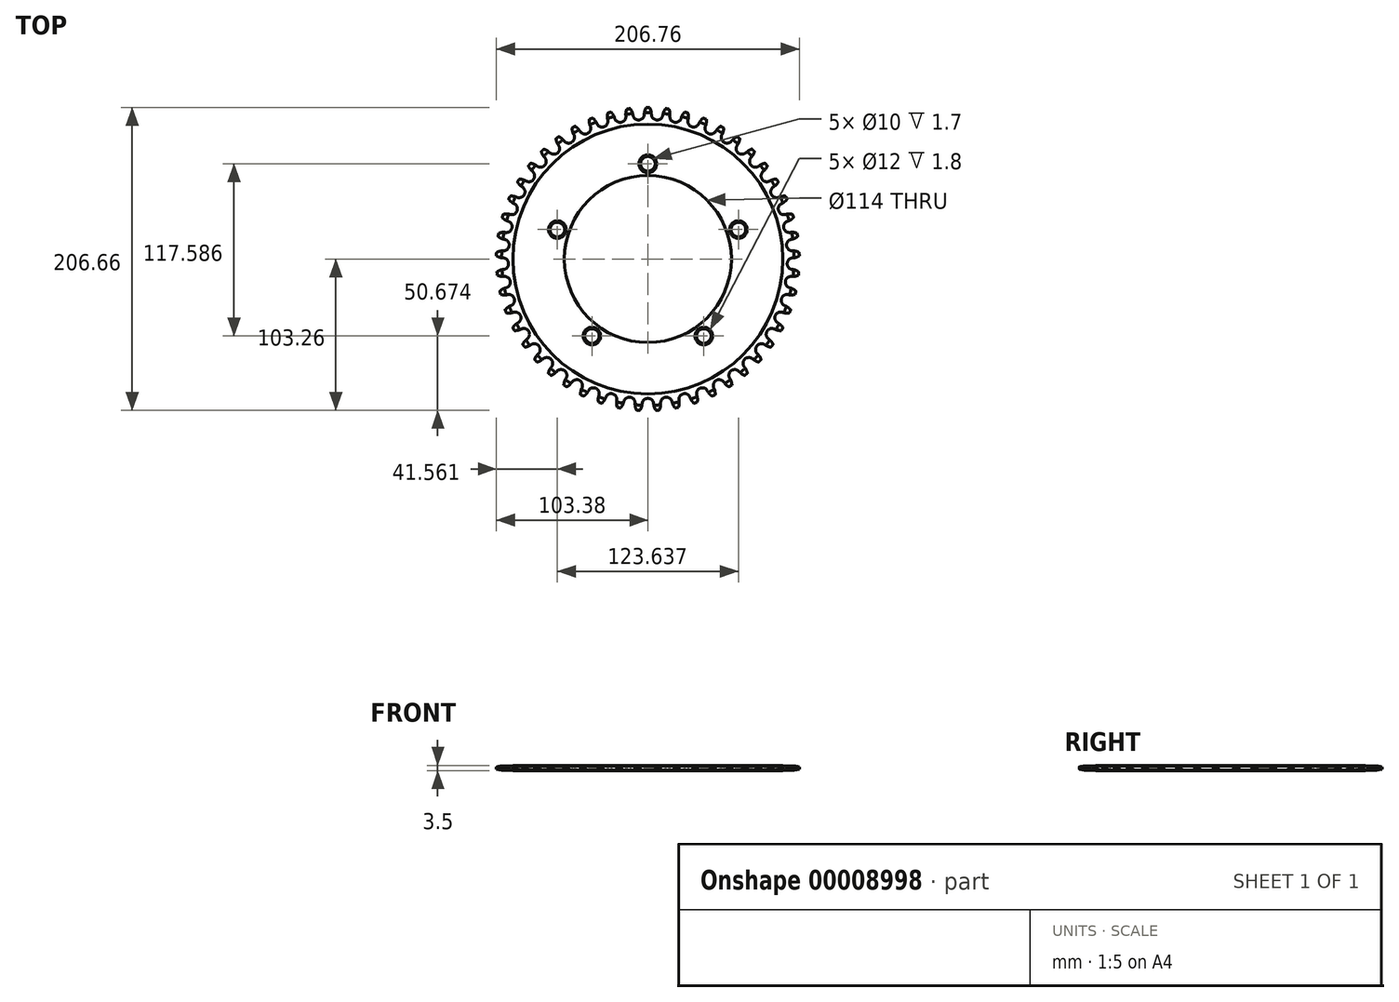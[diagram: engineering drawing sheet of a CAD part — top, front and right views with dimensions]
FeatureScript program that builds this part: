
annotation { "Feature Type Name" : "Feature", "Feature Type Description" : "" }
export const myFeature = defineFeature(function(context is Context, id is Id, definition is map)
    precondition{}
    {
        {
            var Q0;
            Q0=qCreatedBy(makeId("Top.planeOp"),FACE);
            var sketch = newSketch(context, id + "F0", { "sketchPlane" : qUnion([Q0])});
            skArc(sketch, "E0", {"start": v(2.38, 98.9) * mm, "mid": v(3.46, 96.2) * mm, "end": v(6.1, 94.95) * mm});
            skArc(sketch, "E1", {"start": v(-6.1, 94.95) * mm, "mid": v(-3.46, 96.2) * mm, "end": v(-2.38, 98.9) * mm});
            skArc(sketch, "E2", {"start": v(-1.14, 103.4) * mm, "mid": v(-2.06, 101.24) * mm, "end": v(-2.38, 98.9) * mm});
            skArc(sketch, "E3.trimOffspring", {"start": v(2.38, 98.9) * mm, "mid": v(2.06, 101.24) * mm, "end": v(1.14, 103.4) * mm});
            skLineSegment(sketch, "E4.1.1", {"start": v(-6.1, 94.95) * mm, "end": v(0, 0) * mm});
            skLineSegment(sketch, "E4.48.2", {"start": v(0, 0) * mm, "end": v(6.1, 94.95) * mm});
            skPoint(sketch, "E4.center", {"position": v(0, 0) * mm});
            skLineSegment(sketch, "E5", {"start": v(-1.14, 103.4) * mm, "end": v(1.14, 103.4) * mm});
            skPoint(sketch, "E6.orphan", {"position": v(0, 104.9) * mm});
            skLineSegment(sketch, "E7.1.0", {"start": v(0, 0) * mm, "end": v(-6.1, 94.95) * mm});
            skLineSegment(sketch, "E7.1.1", {"start": v(-18.19, 93.39) * mm, "end": v(0, 0) * mm});
            skPoint(sketch, "E7.1.2", {"position": v(-13.41, 104.04) * mm});
            skArc(sketch, "E7.1.4", {"start": v(-18.19, 93.39) * mm, "mid": v(-15.73, 94.96) * mm, "end": v(-15, 97.79) * mm});
            skArc(sketch, "E7.1.5", {"start": v(-10.29, 98.4) * mm, "mid": v(-10.9, 100.67) * mm, "end": v(-12.1, 102.7) * mm});
            skArc(sketch, "E7.1.6", {"start": v(-14.35, 102.4) * mm, "mid": v(-15, 100.14) * mm, "end": v(-15, 97.79) * mm});
            skLineSegment(sketch, "E7.1.7", {"start": v(-14.35, 102.4) * mm, "end": v(-12.1, 102.7) * mm});
            skArc(sketch, "E7.1.8", {"start": v(-10.29, 98.4) * mm, "mid": v(-8.87, 95.84) * mm, "end": v(-6.1, 94.95) * mm});
            skLineSegment(sketch, "E7.2.0", {"start": v(0, 0) * mm, "end": v(-18.19, 93.39) * mm});
            skLineSegment(sketch, "E7.2.1", {"start": v(-29.98, 90.3) * mm, "end": v(0, 0) * mm});
            skPoint(sketch, "E7.2.2", {"position": v(-26.6, 101.47) * mm});
            skArc(sketch, "E7.2.4", {"start": v(-29.98, 90.3) * mm, "mid": v(-27.74, 92.17) * mm, "end": v(-27.4, 95.07) * mm});
            skArc(sketch, "E7.2.5", {"start": v(-22.78, 96.28) * mm, "mid": v(-23.68, 98.45) * mm, "end": v(-25.13, 100.3) * mm});
            skArc(sketch, "E7.2.6", {"start": v(-27.33, 99.73) * mm, "mid": v(-27.68, 97.4) * mm, "end": v(-27.4, 95.07) * mm});
            skLineSegment(sketch, "E7.2.7", {"start": v(-27.33, 99.73) * mm, "end": v(-25.13, 100.3) * mm});
            skArc(sketch, "E7.2.8", {"start": v(-22.78, 96.28) * mm, "mid": v(-21.06, 93.92) * mm, "end": v(-18.19, 93.39) * mm});
            skLineSegment(sketch, "E7.3.0", {"start": v(0, 0) * mm, "end": v(-29.98, 90.3) * mm});
            skLineSegment(sketch, "E7.3.1", {"start": v(-41.28, 85.72) * mm, "end": v(0, 0) * mm});
            skPoint(sketch, "E7.3.2", {"position": v(-39.37, 97.23) * mm});
            skArc(sketch, "E7.3.4", {"start": v(-41.28, 85.72) * mm, "mid": v(-39.3, 87.86) * mm, "end": v(-39.32, 90.78) * mm});
            skArc(sketch, "E7.3.5", {"start": v(-34.9, 92.57) * mm, "mid": v(-36.08, 94.61) * mm, "end": v(-37.75, 96.27) * mm});
            skArc(sketch, "E7.3.6", {"start": v(-39.86, 95.42) * mm, "mid": v(-39.9, 93.06) * mm, "end": v(-39.32, 90.78) * mm});
            skLineSegment(sketch, "E7.3.7", {"start": v(-39.86, 95.42) * mm, "end": v(-37.75, 96.27) * mm});
            skArc(sketch, "E7.3.8", {"start": v(-34.9, 92.57) * mm, "mid": v(-32.9, 90.46) * mm, "end": v(-29.98, 90.3) * mm});
            skLineSegment(sketch, "E7.4.0", {"start": v(0, 0) * mm, "end": v(-41.28, 85.72) * mm});
            skLineSegment(sketch, "E7.4.1", {"start": v(-51.9, 79.74) * mm, "end": v(0, 0) * mm});
            skPoint(sketch, "E7.4.2", {"position": v(-51.48, 91.4) * mm});
            skArc(sketch, "E7.4.4", {"start": v(-51.9, 79.74) * mm, "mid": v(-50.21, 82.12) * mm, "end": v(-50.6, 85.01) * mm});
            skArc(sketch, "E7.4.5", {"start": v(-46.46, 87.35) * mm, "mid": v(-47.88, 89.22) * mm, "end": v(-49.75, 90.65) * mm});
            skArc(sketch, "E7.4.6", {"start": v(-51.73, 89.54) * mm, "mid": v(-51.48, 87.2) * mm, "end": v(-50.6, 85.01) * mm});
            skLineSegment(sketch, "E7.4.7", {"start": v(-51.73, 89.54) * mm, "end": v(-49.75, 90.65) * mm});
            skArc(sketch, "E7.4.8", {"start": v(-46.46, 87.35) * mm, "mid": v(-44.2, 85.5) * mm, "end": v(-41.28, 85.72) * mm});
            skLineSegment(sketch, "E7.5.0", {"start": v(0, 0) * mm, "end": v(-51.9, 79.74) * mm});
            skLineSegment(sketch, "E7.5.1", {"start": v(-61.67, 72.44) * mm, "end": v(0, 0) * mm});
            skPoint(sketch, "E7.5.2", {"position": v(-62.74, 84.07) * mm});
            skArc(sketch, "E7.5.4", {"start": v(-61.67, 72.44) * mm, "mid": v(-60.3, 75.02) * mm, "end": v(-61.07, 77.84) * mm});
            skArc(sketch, "E7.5.5", {"start": v(-57.25, 80.69) * mm, "mid": v(-58.9, 82.37) * mm, "end": v(-60.93, 83.55) * mm});
            skArc(sketch, "E7.5.6", {"start": v(-62.76, 82.19) * mm, "mid": v(-62.2, 79.9) * mm, "end": v(-61.07, 77.84) * mm});
            skLineSegment(sketch, "E7.5.7", {"start": v(-62.76, 82.19) * mm, "end": v(-60.93, 83.55) * mm});
            skArc(sketch, "E7.5.8", {"start": v(-57.25, 80.69) * mm, "mid": v(-54.76, 79.16) * mm, "end": v(-51.9, 79.74) * mm});
            skLineSegment(sketch, "E7.6.0", {"start": v(0, 0) * mm, "end": v(-61.67, 72.44) * mm});
            skLineSegment(sketch, "E7.6.1", {"start": v(-70.43, 63.96) * mm, "end": v(0, 0) * mm});
            skPoint(sketch, "E7.6.2", {"position": v(-72.98, 75.35) * mm});
            skArc(sketch, "E7.6.4", {"start": v(-70.43, 63.96) * mm, "mid": v(-69.4, 66.7) * mm, "end": v(-70.52, 69.4) * mm});
            skArc(sketch, "E7.6.5", {"start": v(-67.1, 72.7) * mm, "mid": v(-68.95, 74.16) * mm, "end": v(-71.12, 75.07) * mm});
            skArc(sketch, "E7.6.6", {"start": v(-72.75, 73.49) * mm, "mid": v(-71.91, 71.29) * mm, "end": v(-70.52, 69.4) * mm});
            skLineSegment(sketch, "E7.6.7", {"start": v(-72.75, 73.49) * mm, "end": v(-71.12, 75.07) * mm});
            skArc(sketch, "E7.6.8", {"start": v(-67.1, 72.7) * mm, "mid": v(-64.44, 71.5) * mm, "end": v(-61.67, 72.44) * mm});
            skLineSegment(sketch, "E7.7.0", {"start": v(0, 0) * mm, "end": v(-70.43, 63.96) * mm});
            skLineSegment(sketch, "E7.7.1", {"start": v(-78.03, 54.43) * mm, "end": v(0, 0) * mm});
            skPoint(sketch, "E7.7.2", {"position": v(-82.01, 65.4) * mm});
            skArc(sketch, "E7.7.4", {"start": v(-78.03, 54.43) * mm, "mid": v(-77.36, 57.27) * mm, "end": v(-78.81, 59.8) * mm});
            skArc(sketch, "E7.7.5", {"start": v(-75.84, 63.53) * mm, "mid": v(-77.86, 64.73) * mm, "end": v(-80.13, 65.36) * mm});
            skArc(sketch, "E7.7.6", {"start": v(-81.55, 63.58) * mm, "mid": v(-80.44, 61.5) * mm, "end": v(-78.81, 59.8) * mm});
            skLineSegment(sketch, "E7.7.7", {"start": v(-81.55, 63.58) * mm, "end": v(-80.13, 65.36) * mm});
            skArc(sketch, "E7.7.8", {"start": v(-75.84, 63.53) * mm, "mid": v(-73.05, 62.68) * mm, "end": v(-70.43, 63.96) * mm});
            skLineSegment(sketch, "E7.8.0", {"start": v(0, 0) * mm, "end": v(-78.03, 54.43) * mm});
            skLineSegment(sketch, "E7.8.1", {"start": v(-84.35, 44) * mm, "end": v(0, 0) * mm});
            skPoint(sketch, "E7.8.2", {"position": v(-89.7, 54.38) * mm});
            skArc(sketch, "E7.8.4", {"start": v(-84.35, 44) * mm, "mid": v(-84.05, 46.91) * mm, "end": v(-85.81, 49.24) * mm});
            skArc(sketch, "E7.8.5", {"start": v(-83.34, 53.3) * mm, "mid": v(-85.5, 54.25) * mm, "end": v(-87.83, 54.57) * mm});
            skArc(sketch, "E7.8.6", {"start": v(-89.01, 52.63) * mm, "mid": v(-87.64, 50.72) * mm, "end": v(-85.81, 49.24) * mm});
            skLineSegment(sketch, "E7.8.7", {"start": v(-89.01, 52.63) * mm, "end": v(-87.83, 54.57) * mm});
            skArc(sketch, "E7.8.8", {"start": v(-83.34, 53.3) * mm, "mid": v(-80.47, 52.82) * mm, "end": v(-78.03, 54.43) * mm});
            skLineSegment(sketch, "E7.9.0", {"start": v(0, 0) * mm, "end": v(-84.35, 44) * mm});
            skLineSegment(sketch, "E7.9.1", {"start": v(-89.29, 32.86) * mm, "end": v(0, 0) * mm});
            skPoint(sketch, "E7.9.2", {"position": v(-95.92, 42.46) * mm});
            skArc(sketch, "E7.9.4", {"start": v(-89.29, 32.86) * mm, "mid": v(-89.36, 35.78) * mm, "end": v(-91.4, 37.86) * mm});
            skArc(sketch, "E7.9.5", {"start": v(-89.48, 42.21) * mm, "mid": v(-91.74, 42.87) * mm, "end": v(-94.09, 42.9) * mm});
            skArc(sketch, "E7.9.6", {"start": v(-95, 40.81) * mm, "mid": v(-93.4, 39.1) * mm, "end": v(-91.4, 37.86) * mm});
            skLineSegment(sketch, "E7.9.7", {"start": v(-95, 40.81) * mm, "end": v(-94.09, 42.9) * mm});
            skArc(sketch, "E7.9.8", {"start": v(-89.48, 42.21) * mm, "mid": v(-86.56, 42.1) * mm, "end": v(-84.35, 44) * mm});
            skLineSegment(sketch, "E7.10.0", {"start": v(0, 0) * mm, "end": v(-89.29, 32.86) * mm});
            skLineSegment(sketch, "E7.10.1", {"start": v(-92.76, 21.17) * mm, "end": v(0, 0) * mm});
            skPoint(sketch, "E7.10.2", {"position": v(-100.56, 29.85) * mm});
            skArc(sketch, "E7.10.4", {"start": v(-92.76, 21.17) * mm, "mid": v(-93.2, 24.06) * mm, "end": v(-95.5, 25.86) * mm});
            skArc(sketch, "E7.10.5", {"start": v(-94.14, 30.42) * mm, "mid": v(-96.47, 30.78) * mm, "end": v(-98.8, 30.5) * mm});
            skArc(sketch, "E7.10.6", {"start": v(-99.45, 28.33) * mm, "mid": v(-97.64, 26.83) * mm, "end": v(-95.5, 25.86) * mm});
            skLineSegment(sketch, "E7.10.7", {"start": v(-99.45, 28.33) * mm, "end": v(-98.8, 30.5) * mm});
            skArc(sketch, "E7.10.8", {"start": v(-94.14, 30.42) * mm, "mid": v(-91.23, 30.68) * mm, "end": v(-89.29, 32.86) * mm});
            skLineSegment(sketch, "E7.11.0", {"start": v(0, 0) * mm, "end": v(-92.76, 21.17) * mm});
            skLineSegment(sketch, "E7.11.1", {"start": v(-94.7, 9.14) * mm, "end": v(0, 0) * mm});
            skPoint(sketch, "E7.11.2", {"position": v(-103.55, 16.74) * mm});
            skArc(sketch, "E7.11.4", {"start": v(-94.7, 9.14) * mm, "mid": v(-95.5, 11.94) * mm, "end": v(-98.02, 13.43) * mm});
            skArc(sketch, "E7.11.5", {"start": v(-97.26, 18.14) * mm, "mid": v(-99.61, 18.2) * mm, "end": v(-101.9, 17.62) * mm});
            skArc(sketch, "E7.11.6", {"start": v(-102.26, 15.38) * mm, "mid": v(-100.27, 14.12) * mm, "end": v(-98.02, 13.43) * mm});
            skLineSegment(sketch, "E7.11.7", {"start": v(-102.26, 15.38) * mm, "end": v(-101.9, 17.62) * mm});
            skArc(sketch, "E7.11.8", {"start": v(-97.26, 18.14) * mm, "mid": v(-94.4, 18.76) * mm, "end": v(-92.76, 21.17) * mm});
            skLineSegment(sketch, "E7.12.0", {"start": v(0, 0) * mm, "end": v(-94.7, 9.14) * mm});
            skLineSegment(sketch, "E7.12.1", {"start": v(-95.1, -3.05) * mm, "end": v(0, 0) * mm});
            skPoint(sketch, "E7.12.2", {"position": v(-104.85, 3.36) * mm});
            skArc(sketch, "E7.12.4", {"start": v(-95.1, -3.05) * mm, "mid": v(-96.25, -0.37) * mm, "end": v(-98.93, 0.8) * mm});
            skArc(sketch, "E7.12.5", {"start": v(-98.78, 5.55) * mm, "mid": v(-101.12, 5.3) * mm, "end": v(-103.3, 4.45) * mm});
            skArc(sketch, "E7.12.6", {"start": v(-103.38, 2.18) * mm, "mid": v(-101.25, 1.18) * mm, "end": v(-98.93, 0.8) * mm});
            skLineSegment(sketch, "E7.12.7", {"start": v(-103.38, 2.18) * mm, "end": v(-103.3, 4.45) * mm});
            skArc(sketch, "E7.12.8", {"start": v(-98.78, 5.55) * mm, "mid": v(-96.03, 6.54) * mm, "end": v(-94.7, 9.14) * mm});
            skLineSegment(sketch, "E7.13.0", {"start": v(0, 0) * mm, "end": v(-95.1, -3.05) * mm});
            skLineSegment(sketch, "E7.13.1", {"start": v(-93.92, -15.18) * mm, "end": v(0, 0) * mm});
            skPoint(sketch, "E7.13.2", {"position": v(-104.41, -10.07) * mm});
            skArc(sketch, "E7.13.4", {"start": v(-93.92, -15.18) * mm, "mid": v(-95.42, -12.68) * mm, "end": v(-98.22, -11.87) * mm});
            skArc(sketch, "E7.13.5", {"start": v(-98.68, -7.13) * mm, "mid": v(-100.97, -7.67) * mm, "end": v(-103.03, -8.8) * mm});
            skArc(sketch, "E7.13.6", {"start": v(-102.81, -11.06) * mm, "mid": v(-100.57, -11.78) * mm, "end": v(-98.22, -11.87) * mm});
            skLineSegment(sketch, "E7.13.7", {"start": v(-102.81, -11.06) * mm, "end": v(-103.03, -8.8) * mm});
            skArc(sketch, "E7.13.8", {"start": v(-98.68, -7.13) * mm, "mid": v(-96.08, -5.8) * mm, "end": v(-95.1, -3.05) * mm});
            skLineSegment(sketch, "E7.14.0", {"start": v(0, 0) * mm, "end": v(-93.92, -15.18) * mm});
            skLineSegment(sketch, "E7.14.1", {"start": v(-91.2, -27.07) * mm, "end": v(0, 0) * mm});
            skPoint(sketch, "E7.14.2", {"position": v(-102.27, -23.34) * mm});
            skArc(sketch, "E7.14.4", {"start": v(-91.2, -27.07) * mm, "mid": v(-93.01, -24.77) * mm, "end": v(-95.9, -24.33) * mm});
            skArc(sketch, "E7.14.5", {"start": v(-96.96, -19.69) * mm, "mid": v(-99.16, -20.51) * mm, "end": v(-101.06, -21.9) * mm});
            skArc(sketch, "E7.14.6", {"start": v(-100.55, -24.12) * mm, "mid": v(-98.24, -24.54) * mm, "end": v(-95.9, -24.33) * mm});
            skLineSegment(sketch, "E7.14.7", {"start": v(-100.55, -24.12) * mm, "end": v(-101.06, -21.9) * mm});
            skArc(sketch, "E7.14.8", {"start": v(-96.96, -19.69) * mm, "mid": v(-94.55, -18.04) * mm, "end": v(-93.92, -15.18) * mm});
            skLineSegment(sketch, "E7.15.0", {"start": v(0, 0) * mm, "end": v(-91.2, -27.07) * mm});
            skLineSegment(sketch, "E7.15.1", {"start": v(-87, -38.51) * mm, "end": v(0, 0) * mm});
            skPoint(sketch, "E7.15.2", {"position": v(-98.44, -36.23) * mm});
            skArc(sketch, "E7.15.4", {"start": v(-87, -38.51) * mm, "mid": v(-89.08, -36.46) * mm, "end": v(-92, -36.4) * mm});
            skArc(sketch, "E7.15.5", {"start": v(-93.64, -31.92) * mm, "mid": v(-95.72, -33.03) * mm, "end": v(-97.43, -34.64) * mm});
            skArc(sketch, "E7.15.6", {"start": v(-96.64, -36.78) * mm, "mid": v(-94.3, -36.9) * mm, "end": v(-92, -36.4) * mm});
            skLineSegment(sketch, "E7.15.7", {"start": v(-96.64, -36.78) * mm, "end": v(-97.43, -34.64) * mm});
            skArc(sketch, "E7.15.8", {"start": v(-93.64, -31.92) * mm, "mid": v(-91.47, -29.98) * mm, "end": v(-91.2, -27.07) * mm});
            skLineSegment(sketch, "E7.16.0", {"start": v(0, 0) * mm, "end": v(-87, -38.51) * mm});
            skLineSegment(sketch, "E7.16.1", {"start": v(-81.36, -49.32) * mm, "end": v(0, 0) * mm});
            skPoint(sketch, "E7.16.2", {"position": v(-93, -48.52) * mm});
            skArc(sketch, "E7.16.4", {"start": v(-81.36, -49.32) * mm, "mid": v(-83.69, -47.56) * mm, "end": v(-86.59, -47.86) * mm});
            skArc(sketch, "E7.16.5", {"start": v(-88.8, -43.64) * mm, "mid": v(-90.71, -45) * mm, "end": v(-92.2, -46.82) * mm});
            skArc(sketch, "E7.16.6", {"start": v(-91.15, -48.83) * mm, "mid": v(-88.8, -48.66) * mm, "end": v(-86.59, -47.86) * mm});
            skLineSegment(sketch, "E7.16.7", {"start": v(-91.15, -48.83) * mm, "end": v(-92.2, -46.82) * mm});
            skArc(sketch, "E7.16.8", {"start": v(-88.8, -43.64) * mm, "mid": v(-86.88, -41.43) * mm, "end": v(-87, -38.51) * mm});
            skLineSegment(sketch, "E7.17.0", {"start": v(0, 0) * mm, "end": v(-81.36, -49.32) * mm});
            skLineSegment(sketch, "E7.17.1", {"start": v(-74.38, -59.32) * mm, "end": v(0, 0) * mm});
            skPoint(sketch, "E7.17.2", {"position": v(-86.04, -60.01) * mm});
            skArc(sketch, "E7.17.4", {"start": v(-74.38, -59.32) * mm, "mid": v(-76.92, -57.87) * mm, "end": v(-79.76, -58.54) * mm});
            skArc(sketch, "E7.17.5", {"start": v(-82.48, -54.63) * mm, "mid": v(-84.21, -56.23) * mm, "end": v(-85.46, -58.22) * mm});
            skArc(sketch, "E7.17.6", {"start": v(-84.15, -60.09) * mm, "mid": v(-81.85, -59.61) * mm, "end": v(-79.76, -58.54) * mm});
            skLineSegment(sketch, "E7.17.7", {"start": v(-84.15, -60.09) * mm, "end": v(-85.46, -58.22) * mm});
            skArc(sketch, "E7.17.8", {"start": v(-82.48, -54.63) * mm, "mid": v(-80.87, -52.2) * mm, "end": v(-81.36, -49.32) * mm});
            skLineSegment(sketch, "E7.18.0", {"start": v(0, 0) * mm, "end": v(-74.38, -59.32) * mm});
            skLineSegment(sketch, "E7.18.1", {"start": v(-66.19, -68.34) * mm, "end": v(0, 0) * mm});
            skPoint(sketch, "E7.18.2", {"position": v(-77.65, -70.52) * mm});
            skArc(sketch, "E7.18.4", {"start": v(-66.19, -68.34) * mm, "mid": v(-68.89, -67.23) * mm, "end": v(-71.62, -68.26) * mm});
            skArc(sketch, "E7.18.5", {"start": v(-74.82, -64.73) * mm, "mid": v(-76.33, -66.53) * mm, "end": v(-77.3, -68.67) * mm});
            skArc(sketch, "E7.18.6", {"start": v(-75.78, -70.36) * mm, "mid": v(-73.56, -69.6) * mm, "end": v(-71.62, -68.26) * mm});
            skLineSegment(sketch, "E7.18.7", {"start": v(-75.78, -70.36) * mm, "end": v(-77.3, -68.67) * mm});
            skArc(sketch, "E7.18.8", {"start": v(-74.82, -64.73) * mm, "mid": v(-73.53, -62.11) * mm, "end": v(-74.38, -59.32) * mm});
            skLineSegment(sketch, "E7.19.0", {"start": v(0, 0) * mm, "end": v(-66.19, -68.34) * mm});
            skLineSegment(sketch, "E7.19.1", {"start": v(-56.9, -76.25) * mm, "end": v(0, 0) * mm});
            skPoint(sketch, "E7.19.2", {"position": v(-68, -79.87) * mm});
            skArc(sketch, "E7.19.4", {"start": v(-56.9, -76.25) * mm, "mid": v(-59.72, -75.48) * mm, "end": v(-62.3, -76.86) * mm});
            skArc(sketch, "E7.19.5", {"start": v(-65.93, -73.77) * mm, "mid": v(-67.2, -75.75) * mm, "end": v(-67.9, -78) * mm});
            skArc(sketch, "E7.19.6", {"start": v(-66.16, -79.47) * mm, "mid": v(-64.05, -78.42) * mm, "end": v(-62.3, -76.86) * mm});
            skLineSegment(sketch, "E7.19.7", {"start": v(-66.16, -79.47) * mm, "end": v(-67.9, -78) * mm});
            skArc(sketch, "E7.19.8", {"start": v(-65.93, -73.77) * mm, "mid": v(-64.98, -71) * mm, "end": v(-66.19, -68.34) * mm});
            skLineSegment(sketch, "E7.20.0", {"start": v(0, 0) * mm, "end": v(-56.9, -76.25) * mm});
            skLineSegment(sketch, "E7.20.1", {"start": v(-46.69, -82.9) * mm, "end": v(0, 0) * mm});
            skPoint(sketch, "E7.20.2", {"position": v(-57.23, -87.91) * mm});
            skArc(sketch, "E7.20.4", {"start": v(-46.69, -82.9) * mm, "mid": v(-49.58, -82.5) * mm, "end": v(-51.96, -84.2) * mm});
            skArc(sketch, "E7.20.5", {"start": v(-55.95, -81.6) * mm, "mid": v(-56.96, -83.72) * mm, "end": v(-57.36, -86.04) * mm});
            skArc(sketch, "E7.20.6", {"start": v(-55.46, -87.28) * mm, "mid": v(-53.5, -85.97) * mm, "end": v(-51.96, -84.2) * mm});
            skLineSegment(sketch, "E7.20.7", {"start": v(-55.46, -87.28) * mm, "end": v(-57.36, -86.04) * mm});
            skArc(sketch, "E7.20.8", {"start": v(-55.95, -81.6) * mm, "mid": v(-55.37, -78.73) * mm, "end": v(-56.9, -76.25) * mm});
            skLineSegment(sketch, "E7.21.0", {"start": v(0, 0) * mm, "end": v(-46.69, -82.9) * mm});
            skLineSegment(sketch, "E7.21.1", {"start": v(-35.7, -88.19) * mm, "end": v(0, 0) * mm});
            skPoint(sketch, "E7.21.2", {"position": v(-45.51, -94.51) * mm});
            skArc(sketch, "E7.21.4", {"start": v(-35.7, -88.19) * mm, "mid": v(-38.62, -88.16) * mm, "end": v(-40.77, -90.14) * mm});
            skArc(sketch, "E7.21.5", {"start": v(-45.06, -88.08) * mm, "mid": v(-45.79, -90.32) * mm, "end": v(-45.89, -92.67) * mm});
            skArc(sketch, "E7.21.6", {"start": v(-43.84, -93.65) * mm, "mid": v(-42.07, -92.1) * mm, "end": v(-40.77, -90.14) * mm});
            skLineSegment(sketch, "E7.21.7", {"start": v(-43.84, -93.65) * mm, "end": v(-45.89, -92.67) * mm});
            skArc(sketch, "E7.21.8", {"start": v(-45.06, -88.08) * mm, "mid": v(-44.85, -85.17) * mm, "end": v(-46.69, -82.9) * mm});
            skLineSegment(sketch, "E7.22.0", {"start": v(0, 0) * mm, "end": v(-35.7, -88.19) * mm});
            skLineSegment(sketch, "E7.22.1", {"start": v(-24.13, -92.03) * mm, "end": v(0, 0) * mm});
            skPoint(sketch, "E7.22.2", {"position": v(-33.05, -99.56) * mm});
            skArc(sketch, "E7.22.4", {"start": v(-24.13, -92.03) * mm, "mid": v(-27.03, -92.38) * mm, "end": v(-28.9, -94.62) * mm});
            skArc(sketch, "E7.22.5", {"start": v(-33.43, -93.12) * mm, "mid": v(-33.86, -95.43) * mm, "end": v(-33.66, -97.77) * mm});
            skArc(sketch, "E7.22.6", {"start": v(-31.5, -98.49) * mm, "mid": v(-29.94, -96.73) * mm, "end": v(-28.9, -94.62) * mm});
            skLineSegment(sketch, "E7.22.7", {"start": v(-31.5, -98.49) * mm, "end": v(-33.66, -97.77) * mm});
            skArc(sketch, "E7.22.8", {"start": v(-33.43, -93.12) * mm, "mid": v(-33.59, -90.2) * mm, "end": v(-35.7, -88.19) * mm});
            skLineSegment(sketch, "E7.23.0", {"start": v(0, 0) * mm, "end": v(-24.13, -92.03) * mm});
            skLineSegment(sketch, "E7.23.1", {"start": v(-12.17, -94.36) * mm, "end": v(0, 0) * mm});
            skPoint(sketch, "E7.23.2", {"position": v(-20.05, -102.96) * mm});
            skArc(sketch, "E7.23.4", {"start": v(-12.17, -94.36) * mm, "mid": v(-15, -95.08) * mm, "end": v(-16.57, -97.54) * mm});
            skArc(sketch, "E7.23.5", {"start": v(-21.24, -96.63) * mm, "mid": v(-21.38, -98.98) * mm, "end": v(-20.88, -101.28) * mm});
            skArc(sketch, "E7.23.6", {"start": v(-18.65, -101.7) * mm, "mid": v(-17.33, -99.77) * mm, "end": v(-16.57, -97.54) * mm});
            skLineSegment(sketch, "E7.23.7", {"start": v(-18.65, -101.7) * mm, "end": v(-20.88, -101.28) * mm});
            skArc(sketch, "E7.23.8", {"start": v(-21.24, -96.63) * mm, "mid": v(-21.78, -93.76) * mm, "end": v(-24.13, -92.03) * mm});
            skLineSegment(sketch, "E7.24.0", {"start": v(0, 0) * mm, "end": v(-12.17, -94.36) * mm});
            skLineSegment(sketch, "E7.24.1", {"start": v(0, -95.14) * mm, "end": v(0, 0) * mm});
            skPoint(sketch, "E7.24.2", {"position": v(-6.72, -104.68) * mm});
            skArc(sketch, "E7.24.4", {"start": v(0, -95.14) * mm, "mid": v(-2.71, -96.22) * mm, "end": v(-3.96, -98.86) * mm});
            skArc(sketch, "E7.24.5", {"start": v(-8.71, -98.55) * mm, "mid": v(-8.55, -100.9) * mm, "end": v(-7.76, -103.11) * mm});
            skArc(sketch, "E7.24.6", {"start": v(-5.5, -103.26) * mm, "mid": v(-4.43, -101.16) * mm, "end": v(-3.96, -98.86) * mm});
            skLineSegment(sketch, "E7.24.7", {"start": v(-5.5, -103.26) * mm, "end": v(-7.76, -103.11) * mm});
            skArc(sketch, "E7.24.8", {"start": v(-8.71, -98.55) * mm, "mid": v(-9.61, -95.77) * mm, "end": v(-12.17, -94.36) * mm});
            skLineSegment(sketch, "E7.25.0", {"start": v(0, 0) * mm, "end": v(0, -95.14) * mm});
            skLineSegment(sketch, "E7.25.1", {"start": v(12.17, -94.36) * mm, "end": v(0, 0) * mm});
            skPoint(sketch, "E7.25.2", {"position": v(6.72, -104.68) * mm});
            skArc(sketch, "E7.25.4", {"start": v(12.17, -94.36) * mm, "mid": v(9.61, -95.77) * mm, "end": v(8.71, -98.55) * mm});
            skArc(sketch, "E7.25.5", {"start": v(3.96, -98.86) * mm, "mid": v(4.43, -101.16) * mm, "end": v(5.5, -103.26) * mm});
            skArc(sketch, "E7.25.6", {"start": v(7.76, -103.11) * mm, "mid": v(8.55, -100.9) * mm, "end": v(8.71, -98.55) * mm});
            skLineSegment(sketch, "E7.25.7", {"start": v(7.76, -103.11) * mm, "end": v(5.5, -103.26) * mm});
            skArc(sketch, "E7.25.8", {"start": v(3.96, -98.86) * mm, "mid": v(2.71, -96.22) * mm, "end": v(0, -95.14) * mm});
            skLineSegment(sketch, "E7.26.0", {"start": v(0, 0) * mm, "end": v(12.17, -94.36) * mm});
            skLineSegment(sketch, "E7.26.1", {"start": v(24.13, -92.03) * mm, "end": v(0, 0) * mm});
            skPoint(sketch, "E7.26.2", {"position": v(20.05, -102.96) * mm});
            skArc(sketch, "E7.26.4", {"start": v(24.13, -92.03) * mm, "mid": v(21.78, -93.76) * mm, "end": v(21.24, -96.63) * mm});
            skArc(sketch, "E7.26.5", {"start": v(16.57, -97.54) * mm, "mid": v(17.33, -99.77) * mm, "end": v(18.65, -101.7) * mm});
            skArc(sketch, "E7.26.6", {"start": v(20.88, -101.28) * mm, "mid": v(21.38, -98.98) * mm, "end": v(21.24, -96.63) * mm});
            skLineSegment(sketch, "E7.26.7", {"start": v(20.88, -101.28) * mm, "end": v(18.65, -101.7) * mm});
            skArc(sketch, "E7.26.8", {"start": v(16.57, -97.54) * mm, "mid": v(15, -95.08) * mm, "end": v(12.17, -94.36) * mm});
            skLineSegment(sketch, "E7.27.0", {"start": v(0, 0) * mm, "end": v(24.13, -92.03) * mm});
            skLineSegment(sketch, "E7.27.1", {"start": v(35.7, -88.19) * mm, "end": v(0, 0) * mm});
            skPoint(sketch, "E7.27.2", {"position": v(33.05, -99.56) * mm});
            skArc(sketch, "E7.27.4", {"start": v(35.7, -88.19) * mm, "mid": v(33.59, -90.2) * mm, "end": v(33.43, -93.12) * mm});
            skArc(sketch, "E7.27.5", {"start": v(28.9, -94.62) * mm, "mid": v(29.94, -96.73) * mm, "end": v(31.5, -98.49) * mm});
            skArc(sketch, "E7.27.6", {"start": v(33.66, -97.77) * mm, "mid": v(33.86, -95.43) * mm, "end": v(33.43, -93.12) * mm});
            skLineSegment(sketch, "E7.27.7", {"start": v(33.66, -97.77) * mm, "end": v(31.5, -98.49) * mm});
            skArc(sketch, "E7.27.8", {"start": v(28.9, -94.62) * mm, "mid": v(27.03, -92.38) * mm, "end": v(24.13, -92.03) * mm});
            skLineSegment(sketch, "E7.28.0", {"start": v(0, 0) * mm, "end": v(35.7, -88.19) * mm});
            skLineSegment(sketch, "E7.28.1", {"start": v(46.69, -82.9) * mm, "end": v(0, 0) * mm});
            skPoint(sketch, "E7.28.2", {"position": v(45.51, -94.51) * mm});
            skArc(sketch, "E7.28.4", {"start": v(46.69, -82.9) * mm, "mid": v(44.85, -85.17) * mm, "end": v(45.06, -88.08) * mm});
            skArc(sketch, "E7.28.5", {"start": v(40.77, -90.14) * mm, "mid": v(42.07, -92.1) * mm, "end": v(43.84, -93.65) * mm});
            skArc(sketch, "E7.28.6", {"start": v(45.89, -92.67) * mm, "mid": v(45.79, -90.32) * mm, "end": v(45.06, -88.08) * mm});
            skLineSegment(sketch, "E7.28.7", {"start": v(45.89, -92.67) * mm, "end": v(43.84, -93.65) * mm});
            skArc(sketch, "E7.28.8", {"start": v(40.77, -90.14) * mm, "mid": v(38.62, -88.16) * mm, "end": v(35.7, -88.19) * mm});
            skLineSegment(sketch, "E7.29.0", {"start": v(0, 0) * mm, "end": v(46.69, -82.9) * mm});
            skLineSegment(sketch, "E7.29.1", {"start": v(56.9, -76.25) * mm, "end": v(0, 0) * mm});
            skPoint(sketch, "E7.29.2", {"position": v(57.23, -87.91) * mm});
            skArc(sketch, "E7.29.4", {"start": v(56.9, -76.25) * mm, "mid": v(55.37, -78.73) * mm, "end": v(55.95, -81.6) * mm});
            skArc(sketch, "E7.29.5", {"start": v(51.96, -84.2) * mm, "mid": v(53.5, -85.97) * mm, "end": v(55.46, -87.28) * mm});
            skArc(sketch, "E7.29.6", {"start": v(57.36, -86.04) * mm, "mid": v(56.96, -83.72) * mm, "end": v(55.95, -81.6) * mm});
            skLineSegment(sketch, "E7.29.7", {"start": v(57.36, -86.04) * mm, "end": v(55.46, -87.28) * mm});
            skArc(sketch, "E7.29.8", {"start": v(51.96, -84.2) * mm, "mid": v(49.58, -82.5) * mm, "end": v(46.69, -82.9) * mm});
            skLineSegment(sketch, "E7.30.0", {"start": v(0, 0) * mm, "end": v(56.9, -76.25) * mm});
            skLineSegment(sketch, "E7.30.1", {"start": v(66.19, -68.34) * mm, "end": v(0, 0) * mm});
            skPoint(sketch, "E7.30.2", {"position": v(68, -79.87) * mm});
            skArc(sketch, "E7.30.4", {"start": v(66.19, -68.34) * mm, "mid": v(64.98, -71) * mm, "end": v(65.93, -73.77) * mm});
            skArc(sketch, "E7.30.5", {"start": v(62.3, -76.86) * mm, "mid": v(64.05, -78.42) * mm, "end": v(66.16, -79.47) * mm});
            skArc(sketch, "E7.30.6", {"start": v(67.9, -78) * mm, "mid": v(67.2, -75.75) * mm, "end": v(65.93, -73.77) * mm});
            skLineSegment(sketch, "E7.30.7", {"start": v(67.9, -78) * mm, "end": v(66.16, -79.47) * mm});
            skArc(sketch, "E7.30.8", {"start": v(62.3, -76.86) * mm, "mid": v(59.72, -75.48) * mm, "end": v(56.9, -76.25) * mm});
            skLineSegment(sketch, "E7.31.0", {"start": v(0, 0) * mm, "end": v(66.19, -68.34) * mm});
            skLineSegment(sketch, "E7.31.1", {"start": v(74.38, -59.32) * mm, "end": v(0, 0) * mm});
            skPoint(sketch, "E7.31.2", {"position": v(77.65, -70.52) * mm});
            skArc(sketch, "E7.31.4", {"start": v(74.38, -59.32) * mm, "mid": v(73.53, -62.11) * mm, "end": v(74.82, -64.73) * mm});
            skArc(sketch, "E7.31.5", {"start": v(71.62, -68.26) * mm, "mid": v(73.56, -69.6) * mm, "end": v(75.78, -70.36) * mm});
            skArc(sketch, "E7.31.6", {"start": v(77.3, -68.67) * mm, "mid": v(76.33, -66.53) * mm, "end": v(74.82, -64.73) * mm});
            skLineSegment(sketch, "E7.31.7", {"start": v(77.3, -68.67) * mm, "end": v(75.78, -70.36) * mm});
            skArc(sketch, "E7.31.8", {"start": v(71.62, -68.26) * mm, "mid": v(68.89, -67.23) * mm, "end": v(66.19, -68.34) * mm});
            skLineSegment(sketch, "E7.32.0", {"start": v(0, 0) * mm, "end": v(74.38, -59.32) * mm});
            skLineSegment(sketch, "E7.32.1", {"start": v(81.36, -49.32) * mm, "end": v(0, 0) * mm});
            skPoint(sketch, "E7.32.2", {"position": v(86.04, -60.01) * mm});
            skArc(sketch, "E7.32.4", {"start": v(81.36, -49.32) * mm, "mid": v(80.87, -52.2) * mm, "end": v(82.48, -54.63) * mm});
            skArc(sketch, "E7.32.5", {"start": v(79.76, -58.54) * mm, "mid": v(81.85, -59.61) * mm, "end": v(84.15, -60.09) * mm});
            skArc(sketch, "E7.32.6", {"start": v(85.46, -58.22) * mm, "mid": v(84.21, -56.23) * mm, "end": v(82.48, -54.63) * mm});
            skLineSegment(sketch, "E7.32.7", {"start": v(85.46, -58.22) * mm, "end": v(84.15, -60.09) * mm});
            skArc(sketch, "E7.32.8", {"start": v(79.76, -58.54) * mm, "mid": v(76.92, -57.87) * mm, "end": v(74.38, -59.32) * mm});
            skLineSegment(sketch, "E7.33.0", {"start": v(0, 0) * mm, "end": v(81.36, -49.32) * mm});
            skLineSegment(sketch, "E7.33.1", {"start": v(87, -38.51) * mm, "end": v(0, 0) * mm});
            skPoint(sketch, "E7.33.2", {"position": v(93, -48.52) * mm});
            skArc(sketch, "E7.33.4", {"start": v(87, -38.51) * mm, "mid": v(86.88, -41.43) * mm, "end": v(88.8, -43.64) * mm});
            skArc(sketch, "E7.33.5", {"start": v(86.59, -47.86) * mm, "mid": v(88.8, -48.66) * mm, "end": v(91.15, -48.83) * mm});
            skArc(sketch, "E7.33.6", {"start": v(92.2, -46.82) * mm, "mid": v(90.71, -45) * mm, "end": v(88.8, -43.64) * mm});
            skLineSegment(sketch, "E7.33.7", {"start": v(92.2, -46.82) * mm, "end": v(91.15, -48.83) * mm});
            skArc(sketch, "E7.33.8", {"start": v(86.59, -47.86) * mm, "mid": v(83.69, -47.56) * mm, "end": v(81.36, -49.32) * mm});
            skLineSegment(sketch, "E7.34.0", {"start": v(0, 0) * mm, "end": v(87, -38.51) * mm});
            skLineSegment(sketch, "E7.34.1", {"start": v(91.2, -27.07) * mm, "end": v(0, 0) * mm});
            skPoint(sketch, "E7.34.2", {"position": v(98.44, -36.23) * mm});
            skArc(sketch, "E7.34.4", {"start": v(91.2, -27.07) * mm, "mid": v(91.47, -29.98) * mm, "end": v(93.64, -31.92) * mm});
            skArc(sketch, "E7.34.5", {"start": v(92, -36.4) * mm, "mid": v(94.3, -36.9) * mm, "end": v(96.64, -36.78) * mm});
            skArc(sketch, "E7.34.6", {"start": v(97.43, -34.64) * mm, "mid": v(95.72, -33.03) * mm, "end": v(93.64, -31.92) * mm});
            skLineSegment(sketch, "E7.34.7", {"start": v(97.43, -34.64) * mm, "end": v(96.64, -36.78) * mm});
            skArc(sketch, "E7.34.8", {"start": v(92, -36.4) * mm, "mid": v(89.08, -36.46) * mm, "end": v(87, -38.51) * mm});
            skLineSegment(sketch, "E7.35.0", {"start": v(0, 0) * mm, "end": v(91.2, -27.07) * mm});
            skLineSegment(sketch, "E7.35.1", {"start": v(93.92, -15.18) * mm, "end": v(0, 0) * mm});
            skPoint(sketch, "E7.35.2", {"position": v(102.27, -23.34) * mm});
            skArc(sketch, "E7.35.4", {"start": v(93.92, -15.18) * mm, "mid": v(94.55, -18.04) * mm, "end": v(96.96, -19.69) * mm});
            skArc(sketch, "E7.35.5", {"start": v(95.9, -24.33) * mm, "mid": v(98.24, -24.54) * mm, "end": v(100.55, -24.12) * mm});
            skArc(sketch, "E7.35.6", {"start": v(101.06, -21.9) * mm, "mid": v(99.16, -20.51) * mm, "end": v(96.96, -19.69) * mm});
            skLineSegment(sketch, "E7.35.7", {"start": v(101.06, -21.9) * mm, "end": v(100.55, -24.12) * mm});
            skArc(sketch, "E7.35.8", {"start": v(95.9, -24.33) * mm, "mid": v(93.01, -24.77) * mm, "end": v(91.2, -27.07) * mm});
            skLineSegment(sketch, "E7.36.0", {"start": v(0, 0) * mm, "end": v(93.92, -15.18) * mm});
            skLineSegment(sketch, "E7.36.1", {"start": v(95.1, -3.05) * mm, "end": v(0, 0) * mm});
            skPoint(sketch, "E7.36.2", {"position": v(104.41, -10.07) * mm});
            skArc(sketch, "E7.36.4", {"start": v(95.1, -3.05) * mm, "mid": v(96.08, -5.8) * mm, "end": v(98.68, -7.13) * mm});
            skArc(sketch, "E7.36.5", {"start": v(98.22, -11.87) * mm, "mid": v(100.57, -11.78) * mm, "end": v(102.81, -11.06) * mm});
            skArc(sketch, "E7.36.6", {"start": v(103.03, -8.8) * mm, "mid": v(100.97, -7.67) * mm, "end": v(98.68, -7.13) * mm});
            skLineSegment(sketch, "E7.36.7", {"start": v(103.03, -8.8) * mm, "end": v(102.81, -11.06) * mm});
            skArc(sketch, "E7.36.8", {"start": v(98.22, -11.87) * mm, "mid": v(95.42, -12.68) * mm, "end": v(93.92, -15.18) * mm});
            skLineSegment(sketch, "E7.37.0", {"start": v(0, 0) * mm, "end": v(95.1, -3.05) * mm});
            skLineSegment(sketch, "E7.37.1", {"start": v(94.7, 9.14) * mm, "end": v(0, 0) * mm});
            skPoint(sketch, "E7.37.2", {"position": v(104.85, 3.36) * mm});
            skArc(sketch, "E7.37.4", {"start": v(94.7, 9.14) * mm, "mid": v(96.03, 6.54) * mm, "end": v(98.78, 5.55) * mm});
            skArc(sketch, "E7.37.5", {"start": v(98.93, 0.8) * mm, "mid": v(101.25, 1.18) * mm, "end": v(103.38, 2.18) * mm});
            skArc(sketch, "E7.37.6", {"start": v(103.3, 4.45) * mm, "mid": v(101.12, 5.3) * mm, "end": v(98.78, 5.55) * mm});
            skLineSegment(sketch, "E7.37.7", {"start": v(103.3, 4.45) * mm, "end": v(103.38, 2.18) * mm});
            skArc(sketch, "E7.37.8", {"start": v(98.93, 0.8) * mm, "mid": v(96.25, -0.37) * mm, "end": v(95.1, -3.05) * mm});
            skLineSegment(sketch, "E7.38.0", {"start": v(0, 0) * mm, "end": v(94.7, 9.14) * mm});
            skLineSegment(sketch, "E7.38.1", {"start": v(92.76, 21.17) * mm, "end": v(0, 0) * mm});
            skPoint(sketch, "E7.38.2", {"position": v(103.55, 16.74) * mm});
            skArc(sketch, "E7.38.4", {"start": v(92.76, 21.17) * mm, "mid": v(94.4, 18.76) * mm, "end": v(97.26, 18.14) * mm});
            skArc(sketch, "E7.38.5", {"start": v(98.02, 13.43) * mm, "mid": v(100.27, 14.12) * mm, "end": v(102.26, 15.38) * mm});
            skArc(sketch, "E7.38.6", {"start": v(101.9, 17.62) * mm, "mid": v(99.61, 18.2) * mm, "end": v(97.26, 18.14) * mm});
            skLineSegment(sketch, "E7.38.7", {"start": v(101.9, 17.62) * mm, "end": v(102.26, 15.38) * mm});
            skArc(sketch, "E7.38.8", {"start": v(98.02, 13.43) * mm, "mid": v(95.5, 11.94) * mm, "end": v(94.7, 9.14) * mm});
            skLineSegment(sketch, "E7.39.0", {"start": v(0, 0) * mm, "end": v(92.76, 21.17) * mm});
            skLineSegment(sketch, "E7.39.1", {"start": v(89.29, 32.86) * mm, "end": v(0, 0) * mm});
            skPoint(sketch, "E7.39.2", {"position": v(100.56, 29.85) * mm});
            skArc(sketch, "E7.39.4", {"start": v(89.29, 32.86) * mm, "mid": v(91.23, 30.68) * mm, "end": v(94.14, 30.42) * mm});
            skArc(sketch, "E7.39.5", {"start": v(95.5, 25.86) * mm, "mid": v(97.64, 26.83) * mm, "end": v(99.45, 28.33) * mm});
            skArc(sketch, "E7.39.6", {"start": v(98.8, 30.5) * mm, "mid": v(96.47, 30.78) * mm, "end": v(94.14, 30.42) * mm});
            skLineSegment(sketch, "E7.39.7", {"start": v(98.8, 30.5) * mm, "end": v(99.45, 28.33) * mm});
            skArc(sketch, "E7.39.8", {"start": v(95.5, 25.86) * mm, "mid": v(93.2, 24.06) * mm, "end": v(92.76, 21.17) * mm});
            skLineSegment(sketch, "E7.40.0", {"start": v(0, 0) * mm, "end": v(89.29, 32.86) * mm});
            skLineSegment(sketch, "E7.40.1", {"start": v(84.35, 44) * mm, "end": v(0, 0) * mm});
            skPoint(sketch, "E7.40.2", {"position": v(95.92, 42.46) * mm});
            skArc(sketch, "E7.40.4", {"start": v(84.35, 44) * mm, "mid": v(86.56, 42.1) * mm, "end": v(89.48, 42.21) * mm});
            skArc(sketch, "E7.40.5", {"start": v(91.4, 37.86) * mm, "mid": v(93.4, 39.1) * mm, "end": v(95, 40.81) * mm});
            skArc(sketch, "E7.40.6", {"start": v(94.09, 42.9) * mm, "mid": v(91.74, 42.87) * mm, "end": v(89.48, 42.21) * mm});
            skLineSegment(sketch, "E7.40.7", {"start": v(94.09, 42.9) * mm, "end": v(95, 40.81) * mm});
            skArc(sketch, "E7.40.8", {"start": v(91.4, 37.86) * mm, "mid": v(89.36, 35.78) * mm, "end": v(89.29, 32.86) * mm});
            skLineSegment(sketch, "E7.41.0", {"start": v(0, 0) * mm, "end": v(84.35, 44) * mm});
            skLineSegment(sketch, "E7.41.1", {"start": v(78.03, 54.43) * mm, "end": v(0, 0) * mm});
            skPoint(sketch, "E7.41.2", {"position": v(89.7, 54.38) * mm});
            skArc(sketch, "E7.41.4", {"start": v(78.03, 54.43) * mm, "mid": v(80.47, 52.82) * mm, "end": v(83.34, 53.3) * mm});
            skArc(sketch, "E7.41.5", {"start": v(85.81, 49.24) * mm, "mid": v(87.64, 50.72) * mm, "end": v(89.01, 52.63) * mm});
            skArc(sketch, "E7.41.6", {"start": v(87.83, 54.57) * mm, "mid": v(85.5, 54.25) * mm, "end": v(83.34, 53.3) * mm});
            skLineSegment(sketch, "E7.41.7", {"start": v(87.83, 54.57) * mm, "end": v(89.01, 52.63) * mm});
            skArc(sketch, "E7.41.8", {"start": v(85.81, 49.24) * mm, "mid": v(84.05, 46.91) * mm, "end": v(84.35, 44) * mm});
            skLineSegment(sketch, "E7.42.0", {"start": v(0, 0) * mm, "end": v(78.03, 54.43) * mm});
            skLineSegment(sketch, "E7.42.1", {"start": v(70.43, 63.96) * mm, "end": v(0, 0) * mm});
            skPoint(sketch, "E7.42.2", {"position": v(82.01, 65.4) * mm});
            skArc(sketch, "E7.42.4", {"start": v(70.43, 63.96) * mm, "mid": v(73.05, 62.68) * mm, "end": v(75.84, 63.53) * mm});
            skArc(sketch, "E7.42.5", {"start": v(78.81, 59.8) * mm, "mid": v(80.44, 61.5) * mm, "end": v(81.55, 63.58) * mm});
            skArc(sketch, "E7.42.6", {"start": v(80.13, 65.36) * mm, "mid": v(77.86, 64.73) * mm, "end": v(75.84, 63.53) * mm});
            skLineSegment(sketch, "E7.42.7", {"start": v(80.13, 65.36) * mm, "end": v(81.55, 63.58) * mm});
            skArc(sketch, "E7.42.8", {"start": v(78.81, 59.8) * mm, "mid": v(77.36, 57.27) * mm, "end": v(78.03, 54.43) * mm});
            skLineSegment(sketch, "E7.43.0", {"start": v(0, 0) * mm, "end": v(70.43, 63.96) * mm});
            skLineSegment(sketch, "E7.43.1", {"start": v(61.67, 72.44) * mm, "end": v(0, 0) * mm});
            skPoint(sketch, "E7.43.2", {"position": v(72.98, 75.35) * mm});
            skArc(sketch, "E7.43.4", {"start": v(61.67, 72.44) * mm, "mid": v(64.44, 71.5) * mm, "end": v(67.1, 72.7) * mm});
            skArc(sketch, "E7.43.5", {"start": v(70.52, 69.4) * mm, "mid": v(71.91, 71.29) * mm, "end": v(72.75, 73.49) * mm});
            skArc(sketch, "E7.43.6", {"start": v(71.12, 75.07) * mm, "mid": v(68.95, 74.16) * mm, "end": v(67.1, 72.7) * mm});
            skLineSegment(sketch, "E7.43.7", {"start": v(71.12, 75.07) * mm, "end": v(72.75, 73.49) * mm});
            skArc(sketch, "E7.43.8", {"start": v(70.52, 69.4) * mm, "mid": v(69.4, 66.7) * mm, "end": v(70.43, 63.96) * mm});
            skLineSegment(sketch, "E7.44.0", {"start": v(0, 0) * mm, "end": v(61.67, 72.44) * mm});
            skLineSegment(sketch, "E7.44.1", {"start": v(51.9, 79.74) * mm, "end": v(0, 0) * mm});
            skPoint(sketch, "E7.44.2", {"position": v(62.74, 84.07) * mm});
            skArc(sketch, "E7.44.4", {"start": v(51.9, 79.74) * mm, "mid": v(54.76, 79.16) * mm, "end": v(57.25, 80.69) * mm});
            skArc(sketch, "E7.44.5", {"start": v(61.07, 77.84) * mm, "mid": v(62.2, 79.9) * mm, "end": v(62.76, 82.19) * mm});
            skArc(sketch, "E7.44.6", {"start": v(60.93, 83.55) * mm, "mid": v(58.9, 82.37) * mm, "end": v(57.25, 80.69) * mm});
            skLineSegment(sketch, "E7.44.7", {"start": v(60.93, 83.55) * mm, "end": v(62.76, 82.19) * mm});
            skArc(sketch, "E7.44.8", {"start": v(61.07, 77.84) * mm, "mid": v(60.3, 75.02) * mm, "end": v(61.67, 72.44) * mm});
            skLineSegment(sketch, "E7.45.0", {"start": v(0, 0) * mm, "end": v(51.9, 79.74) * mm});
            skLineSegment(sketch, "E7.45.1", {"start": v(41.28, 85.72) * mm, "end": v(0, 0) * mm});
            skPoint(sketch, "E7.45.2", {"position": v(51.48, 91.4) * mm});
            skArc(sketch, "E7.45.4", {"start": v(41.28, 85.72) * mm, "mid": v(44.2, 85.5) * mm, "end": v(46.46, 87.35) * mm});
            skArc(sketch, "E7.45.5", {"start": v(50.6, 85.01) * mm, "mid": v(51.48, 87.2) * mm, "end": v(51.73, 89.54) * mm});
            skArc(sketch, "E7.45.6", {"start": v(49.75, 90.65) * mm, "mid": v(47.88, 89.22) * mm, "end": v(46.46, 87.35) * mm});
            skLineSegment(sketch, "E7.45.7", {"start": v(49.75, 90.65) * mm, "end": v(51.73, 89.54) * mm});
            skArc(sketch, "E7.45.8", {"start": v(50.6, 85.01) * mm, "mid": v(50.21, 82.12) * mm, "end": v(51.9, 79.74) * mm});
            skLineSegment(sketch, "E7.46.0", {"start": v(0, 0) * mm, "end": v(41.28, 85.72) * mm});
            skLineSegment(sketch, "E7.46.1", {"start": v(29.98, 90.3) * mm, "end": v(0, 0) * mm});
            skPoint(sketch, "E7.46.2", {"position": v(39.37, 97.23) * mm});
            skArc(sketch, "E7.46.4", {"start": v(29.98, 90.3) * mm, "mid": v(32.9, 90.46) * mm, "end": v(34.9, 92.57) * mm});
            skArc(sketch, "E7.46.5", {"start": v(39.32, 90.78) * mm, "mid": v(39.9, 93.06) * mm, "end": v(39.86, 95.42) * mm});
            skArc(sketch, "E7.46.6", {"start": v(37.75, 96.27) * mm, "mid": v(36.08, 94.61) * mm, "end": v(34.9, 92.57) * mm});
            skLineSegment(sketch, "E7.46.7", {"start": v(37.75, 96.27) * mm, "end": v(39.86, 95.42) * mm});
            skArc(sketch, "E7.46.8", {"start": v(39.32, 90.78) * mm, "mid": v(39.3, 87.86) * mm, "end": v(41.28, 85.72) * mm});
            skLineSegment(sketch, "E7.47.0", {"start": v(0, 0) * mm, "end": v(29.98, 90.3) * mm});
            skLineSegment(sketch, "E7.47.1", {"start": v(18.19, 93.39) * mm, "end": v(0, 0) * mm});
            skPoint(sketch, "E7.47.2", {"position": v(26.6, 101.47) * mm});
            skArc(sketch, "E7.47.4", {"start": v(18.19, 93.39) * mm, "mid": v(21.06, 93.92) * mm, "end": v(22.78, 96.28) * mm});
            skArc(sketch, "E7.47.5", {"start": v(27.4, 95.07) * mm, "mid": v(27.68, 97.4) * mm, "end": v(27.33, 99.73) * mm});
            skArc(sketch, "E7.47.6", {"start": v(25.13, 100.3) * mm, "mid": v(23.68, 98.45) * mm, "end": v(22.78, 96.28) * mm});
            skLineSegment(sketch, "E7.47.7", {"start": v(25.13, 100.3) * mm, "end": v(27.33, 99.73) * mm});
            skArc(sketch, "E7.47.8", {"start": v(27.4, 95.07) * mm, "mid": v(27.74, 92.17) * mm, "end": v(29.98, 90.3) * mm});
            skLineSegment(sketch, "E7.48.0", {"start": v(0, 0) * mm, "end": v(18.19, 93.39) * mm});
            skLineSegment(sketch, "E7.48.1", {"start": v(6.1, 94.95) * mm, "end": v(0, 0) * mm});
            skPoint(sketch, "E7.48.2", {"position": v(13.41, 104.04) * mm});
            skArc(sketch, "E7.48.4", {"start": v(6.1, 94.95) * mm, "mid": v(8.87, 95.84) * mm, "end": v(10.29, 98.4) * mm});
            skArc(sketch, "E7.48.5", {"start": v(15, 97.79) * mm, "mid": v(15, 100.14) * mm, "end": v(14.35, 102.4) * mm});
            skArc(sketch, "E7.48.6", {"start": v(12.1, 102.7) * mm, "mid": v(10.9, 100.67) * mm, "end": v(10.29, 98.4) * mm});
            skLineSegment(sketch, "E7.48.7", {"start": v(12.1, 102.7) * mm, "end": v(14.35, 102.4) * mm});
            skArc(sketch, "E7.48.8", {"start": v(15, 97.79) * mm, "mid": v(15.73, 94.96) * mm, "end": v(18.19, 93.39) * mm});
            skSolve(sketch);
        }
        {
            var Q0;
            Q0 = qSketchRegion(id + "F0", true);
            extrude(context, id + "F1", {"entities" : qUnion([Q0]), "depth" : 3.5 * mm});
        }
        {
            var Q0;
            Q0=makeQuery(id+"F1.opExtrude","CAP_FACE",FACE,{"disambiguationData":[OSD([sQuery(id+"F0.wireOp",EDGE,"E0"),sQuery(id+"F0.wireOp",EDGE,"E1"),sQuery(id+"F0.wireOp",EDGE,"E2"),sQuery(id+"F0.wireOp",EDGE,"E3.trimOffspring"),sQuery(id+"F0.wireOp",EDGE,"E4.1.0"),sQuery(id+"F0.wireOp",EDGE,"E4.1.3"),sQuery(id+"F0.wireOp",EDGE,"E4.1.4"),sQuery(id+"F0.wireOp",EDGE,"E4.1.5"),sQuery(id+"F0.wireOp",EDGE,"E4.2.0"),sQuery(id+"F0.wireOp",EDGE,"E4.2.3"),sQuery(id+"F0.wireOp",EDGE,"E4.2.4"),sQuery(id+"F0.wireOp",EDGE,"E4.2.5"),sQuery(id+"F0.wireOp",EDGE,"E4.3.0"),sQuery(id+"F0.wireOp",EDGE,"E4.3.3"),sQuery(id+"F0.wireOp",EDGE,"E4.3.4"),sQuery(id+"F0.wireOp",EDGE,"E4.3.5"),sQuery(id+"F0.wireOp",EDGE,"E4.4.0"),sQuery(id+"F0.wireOp",EDGE,"E4.4.3"),sQuery(id+"F0.wireOp",EDGE,"E4.4.4"),sQuery(id+"F0.wireOp",EDGE,"E4.4.5"),sQuery(id+"F0.wireOp",EDGE,"E4.5.0"),sQuery(id+"F0.wireOp",EDGE,"E4.5.3"),sQuery(id+"F0.wireOp",EDGE,"E4.5.4"),sQuery(id+"F0.wireOp",EDGE,"E4.5.5"),sQuery(id+"F0.wireOp",EDGE,"E4.6.0"),sQuery(id+"F0.wireOp",EDGE,"E4.6.3"),sQuery(id+"F0.wireOp",EDGE,"E4.6.4"),sQuery(id+"F0.wireOp",EDGE,"E4.6.5"),sQuery(id+"F0.wireOp",EDGE,"E4.7.0"),sQuery(id+"F0.wireOp",EDGE,"E4.7.3"),sQuery(id+"F0.wireOp",EDGE,"E4.7.4"),sQuery(id+"F0.wireOp",EDGE,"E4.7.5"),sQuery(id+"F0.wireOp",EDGE,"E4.8.0"),sQuery(id+"F0.wireOp",EDGE,"E4.8.3"),sQuery(id+"F0.wireOp",EDGE,"E4.8.4"),sQuery(id+"F0.wireOp",EDGE,"E4.8.5"),sQuery(id+"F0.wireOp",EDGE,"E4.9.0"),sQuery(id+"F0.wireOp",EDGE,"E4.9.3"),sQuery(id+"F0.wireOp",EDGE,"E4.9.4"),sQuery(id+"F0.wireOp",EDGE,"E4.9.5"),sQuery(id+"F0.wireOp",EDGE,"E4.10.0"),sQuery(id+"F0.wireOp",EDGE,"E4.10.3"),sQuery(id+"F0.wireOp",EDGE,"E4.10.4"),sQuery(id+"F0.wireOp",EDGE,"E4.10.5"),sQuery(id+"F0.wireOp",EDGE,"E4.11.0"),sQuery(id+"F0.wireOp",EDGE,"E4.11.3"),sQuery(id+"F0.wireOp",EDGE,"E4.11.4"),sQuery(id+"F0.wireOp",EDGE,"E4.11.5"),sQuery(id+"F0.wireOp",EDGE,"E4.12.0"),sQuery(id+"F0.wireOp",EDGE,"E4.12.3"),sQuery(id+"F0.wireOp",EDGE,"E4.12.4"),sQuery(id+"F0.wireOp",EDGE,"E4.12.5"),sQuery(id+"F0.wireOp",EDGE,"E4.13.0"),sQuery(id+"F0.wireOp",EDGE,"E4.13.3"),sQuery(id+"F0.wireOp",EDGE,"E4.13.4"),sQuery(id+"F0.wireOp",EDGE,"E4.13.5"),sQuery(id+"F0.wireOp",EDGE,"E4.14.0"),sQuery(id+"F0.wireOp",EDGE,"E4.14.3"),sQuery(id+"F0.wireOp",EDGE,"E4.14.4"),sQuery(id+"F0.wireOp",EDGE,"E4.14.5"),sQuery(id+"F0.wireOp",EDGE,"E4.15.0"),sQuery(id+"F0.wireOp",EDGE,"E4.15.3"),sQuery(id+"F0.wireOp",EDGE,"E4.15.4"),sQuery(id+"F0.wireOp",EDGE,"E4.15.5"),sQuery(id+"F0.wireOp",EDGE,"E4.16.0"),sQuery(id+"F0.wireOp",EDGE,"E4.16.3"),sQuery(id+"F0.wireOp",EDGE,"E4.16.4"),sQuery(id+"F0.wireOp",EDGE,"E4.16.5"),sQuery(id+"F0.wireOp",EDGE,"E4.17.0"),sQuery(id+"F0.wireOp",EDGE,"E4.17.3"),sQuery(id+"F0.wireOp",EDGE,"E4.17.4"),sQuery(id+"F0.wireOp",EDGE,"E4.17.5"),sQuery(id+"F0.wireOp",EDGE,"E4.18.0"),sQuery(id+"F0.wireOp",EDGE,"E4.18.3"),sQuery(id+"F0.wireOp",EDGE,"E4.18.4"),sQuery(id+"F0.wireOp",EDGE,"E4.18.5"),sQuery(id+"F0.wireOp",EDGE,"E4.19.0"),sQuery(id+"F0.wireOp",EDGE,"E4.19.3"),sQuery(id+"F0.wireOp",EDGE,"E4.19.4"),sQuery(id+"F0.wireOp",EDGE,"E4.19.5"),sQuery(id+"F0.wireOp",EDGE,"E4.20.0"),sQuery(id+"F0.wireOp",EDGE,"E4.20.3"),sQuery(id+"F0.wireOp",EDGE,"E4.20.4"),sQuery(id+"F0.wireOp",EDGE,"E4.20.5"),sQuery(id+"F0.wireOp",EDGE,"E4.21.0"),sQuery(id+"F0.wireOp",EDGE,"E4.21.3"),sQuery(id+"F0.wireOp",EDGE,"E4.21.4"),sQuery(id+"F0.wireOp",EDGE,"E4.21.5"),sQuery(id+"F0.wireOp",EDGE,"E4.22.0"),sQuery(id+"F0.wireOp",EDGE,"E4.22.3"),sQuery(id+"F0.wireOp",EDGE,"E4.22.4"),sQuery(id+"F0.wireOp",EDGE,"E4.22.5"),sQuery(id+"F0.wireOp",EDGE,"E4.23.0"),sQuery(id+"F0.wireOp",EDGE,"E4.23.3"),sQuery(id+"F0.wireOp",EDGE,"E4.23.4"),sQuery(id+"F0.wireOp",EDGE,"E4.23.5"),sQuery(id+"F0.wireOp",EDGE,"E4.24.0"),sQuery(id+"F0.wireOp",EDGE,"E4.24.3"),sQuery(id+"F0.wireOp",EDGE,"E4.24.4"),sQuery(id+"F0.wireOp",EDGE,"E4.24.5"),sQuery(id+"F0.wireOp",EDGE,"E4.25.0"),sQuery(id+"F0.wireOp",EDGE,"E4.25.3"),sQuery(id+"F0.wireOp",EDGE,"E4.25.4"),sQuery(id+"F0.wireOp",EDGE,"E4.25.5"),sQuery(id+"F0.wireOp",EDGE,"E4.26.0"),sQuery(id+"F0.wireOp",EDGE,"E4.26.3"),sQuery(id+"F0.wireOp",EDGE,"E4.26.4"),sQuery(id+"F0.wireOp",EDGE,"E4.26.5"),sQuery(id+"F0.wireOp",EDGE,"E4.27.0"),sQuery(id+"F0.wireOp",EDGE,"E4.27.3"),sQuery(id+"F0.wireOp",EDGE,"E4.27.4"),sQuery(id+"F0.wireOp",EDGE,"E4.27.5"),sQuery(id+"F0.wireOp",EDGE,"E4.28.0"),sQuery(id+"F0.wireOp",EDGE,"E4.28.3"),sQuery(id+"F0.wireOp",EDGE,"E4.28.4"),sQuery(id+"F0.wireOp",EDGE,"E4.28.5"),sQuery(id+"F0.wireOp",EDGE,"E4.29.0"),sQuery(id+"F0.wireOp",EDGE,"E4.29.3"),sQuery(id+"F0.wireOp",EDGE,"E4.29.4"),sQuery(id+"F0.wireOp",EDGE,"E4.29.5"),sQuery(id+"F0.wireOp",EDGE,"E4.30.0"),sQuery(id+"F0.wireOp",EDGE,"E4.30.3"),sQuery(id+"F0.wireOp",EDGE,"E4.30.4"),sQuery(id+"F0.wireOp",EDGE,"E4.30.5"),sQuery(id+"F0.wireOp",EDGE,"E4.31.0"),sQuery(id+"F0.wireOp",EDGE,"E4.31.3"),sQuery(id+"F0.wireOp",EDGE,"E4.31.4"),sQuery(id+"F0.wireOp",EDGE,"E4.31.5"),sQuery(id+"F0.wireOp",EDGE,"E4.32.0"),sQuery(id+"F0.wireOp",EDGE,"E4.32.3"),sQuery(id+"F0.wireOp",EDGE,"E4.32.4"),sQuery(id+"F0.wireOp",EDGE,"E4.32.5"),sQuery(id+"F0.wireOp",EDGE,"E4.33.0"),sQuery(id+"F0.wireOp",EDGE,"E4.33.3"),sQuery(id+"F0.wireOp",EDGE,"E4.33.4"),sQuery(id+"F0.wireOp",EDGE,"E4.33.5"),sQuery(id+"F0.wireOp",EDGE,"E4.34.0"),sQuery(id+"F0.wireOp",EDGE,"E4.34.3"),sQuery(id+"F0.wireOp",EDGE,"E4.34.4"),sQuery(id+"F0.wireOp",EDGE,"E4.34.5"),sQuery(id+"F0.wireOp",EDGE,"E4.35.0"),sQuery(id+"F0.wireOp",EDGE,"E4.35.3"),sQuery(id+"F0.wireOp",EDGE,"E4.35.4"),sQuery(id+"F0.wireOp",EDGE,"E4.35.5"),sQuery(id+"F0.wireOp",EDGE,"E4.36.0"),sQuery(id+"F0.wireOp",EDGE,"E4.36.3"),sQuery(id+"F0.wireOp",EDGE,"E4.36.4"),sQuery(id+"F0.wireOp",EDGE,"E4.36.5"),sQuery(id+"F0.wireOp",EDGE,"E4.37.0"),sQuery(id+"F0.wireOp",EDGE,"E4.37.3"),sQuery(id+"F0.wireOp",EDGE,"E4.37.4"),sQuery(id+"F0.wireOp",EDGE,"E4.37.5"),sQuery(id+"F0.wireOp",EDGE,"E4.38.0"),sQuery(id+"F0.wireOp",EDGE,"E4.38.3"),sQuery(id+"F0.wireOp",EDGE,"E4.38.4"),sQuery(id+"F0.wireOp",EDGE,"E4.38.5"),sQuery(id+"F0.wireOp",EDGE,"E4.39.0"),sQuery(id+"F0.wireOp",EDGE,"E4.39.3"),sQuery(id+"F0.wireOp",EDGE,"E4.39.4"),sQuery(id+"F0.wireOp",EDGE,"E4.39.5"),sQuery(id+"F0.wireOp",EDGE,"E4.40.0"),sQuery(id+"F0.wireOp",EDGE,"E4.40.3"),sQuery(id+"F0.wireOp",EDGE,"E4.40.4"),sQuery(id+"F0.wireOp",EDGE,"E4.40.5"),sQuery(id+"F0.wireOp",EDGE,"E4.41.0"),sQuery(id+"F0.wireOp",EDGE,"E4.41.3"),sQuery(id+"F0.wireOp",EDGE,"E4.41.4"),sQuery(id+"F0.wireOp",EDGE,"E4.41.5"),sQuery(id+"F0.wireOp",EDGE,"E4.42.0"),sQuery(id+"F0.wireOp",EDGE,"E4.42.3"),sQuery(id+"F0.wireOp",EDGE,"E4.42.4"),sQuery(id+"F0.wireOp",EDGE,"E4.42.5"),sQuery(id+"F0.wireOp",EDGE,"E4.43.0"),sQuery(id+"F0.wireOp",EDGE,"E4.43.3"),sQuery(id+"F0.wireOp",EDGE,"E4.43.4"),sQuery(id+"F0.wireOp",EDGE,"E4.43.5"),sQuery(id+"F0.wireOp",EDGE,"E4.44.0"),sQuery(id+"F0.wireOp",EDGE,"E4.44.3"),sQuery(id+"F0.wireOp",EDGE,"E4.44.4"),sQuery(id+"F0.wireOp",EDGE,"E4.44.5"),sQuery(id+"F0.wireOp",EDGE,"E4.45.0"),sQuery(id+"F0.wireOp",EDGE,"E4.45.3"),sQuery(id+"F0.wireOp",EDGE,"E4.45.4"),sQuery(id+"F0.wireOp",EDGE,"E4.45.5"),sQuery(id+"F0.wireOp",EDGE,"E4.46.0"),sQuery(id+"F0.wireOp",EDGE,"E4.46.3"),sQuery(id+"F0.wireOp",EDGE,"E4.46.4"),sQuery(id+"F0.wireOp",EDGE,"E4.46.5"),sQuery(id+"F0.wireOp",EDGE,"E4.47.0"),sQuery(id+"F0.wireOp",EDGE,"E4.47.3"),sQuery(id+"F0.wireOp",EDGE,"E4.47.4"),sQuery(id+"F0.wireOp",EDGE,"E4.47.5"),sQuery(id+"F0.wireOp",EDGE,"E4.48.0"),sQuery(id+"F0.wireOp",EDGE,"E4.48.3"),sQuery(id+"F0.wireOp",EDGE,"E4.48.4"),sQuery(id+"F0.wireOp",EDGE,"E4.48.5")])],"isStart":false});
            var sketch = newSketch(context, id + "F2", { "sketchPlane" : qUnion([Q0])});
            skCircle(sketch, "E8", {"center": v(0, 65) * mm, "radius": 5 * mm});
            skPoint(sketch, "E9.center", {"position": v(0, 0) * mm});
            skCircle(sketch, "E10", {"center": v(0, 0) * mm, "radius": 57 * mm});
            skLineSegment(sketch, "E11", {"start": v(0, 57) * mm, "end": v(0, 97.5) * mm, "construction": true});
            skLineSegment(sketch, "E12", {"start": v(54.21, 17.61) * mm, "end": v(84.64, 27.5) * mm, "construction": true});
            skCircle(sketch, "E13", {"center": v(0, 65) * mm, "radius": 6 * mm});
            skCircle(sketch, "E14.1.0", {"center": v(-61.82, 20.09) * mm, "radius": 6 * mm});
            skCircle(sketch, "E14.1.1", {"center": v(-61.82, 20.09) * mm, "radius": 5 * mm});
            skCircle(sketch, "E14.2.0", {"center": v(-38.2, -52.59) * mm, "radius": 6 * mm});
            skCircle(sketch, "E14.2.1", {"center": v(-38.2, -52.59) * mm, "radius": 5 * mm});
            skCircle(sketch, "E14.3.0", {"center": v(38.2, -52.59) * mm, "radius": 6 * mm});
            skCircle(sketch, "E14.3.1", {"center": v(38.2, -52.59) * mm, "radius": 5 * mm});
            skCircle(sketch, "E14.4.0", {"center": v(61.82, 20.09) * mm, "radius": 6 * mm});
            skCircle(sketch, "E14.4.1", {"center": v(61.82, 20.09) * mm, "radius": 5 * mm});
            skSolve(sketch);
        }
        {
            var Q0;
            Q0=makeQuery(id+"F2.imprint","IMPRINT",FACE,{"disambiguationData":[TD([[makeQuery(id+"F2.imprint","IMPRINT",EDGE,{"derivedFrom":sQuery(id+"F2.wireOp",EDGE,"E10")}),1.0]])]});
            var Q1;
            Q1=makeQuery(id+"F2.imprint","IMPRINT",FACE,{"disambiguationData":[TD([[makeQuery(id+"F2.imprint","IMPRINT",EDGE,{"derivedFrom":sQuery(id+"F2.wireOp",EDGE,"E14.1.1")}),1.0]])]});
            var Q2;
            Q2=makeQuery(id+"F2.imprint","IMPRINT",FACE,{"disambiguationData":[TD([[makeQuery(id+"F2.imprint","IMPRINT",EDGE,{"derivedFrom":sQuery(id+"F2.wireOp",EDGE,"E8")}),1.0]])]});
            var Q3;
            Q3=makeQuery(id+"F2.imprint","IMPRINT",FACE,{"disambiguationData":[TD([[makeQuery(id+"F2.imprint","IMPRINT",EDGE,{"derivedFrom":sQuery(id+"F2.wireOp",EDGE,"E14.4.1")}),1.0]])]});
            var Q4;
            Q4=makeQuery(id+"F2.imprint","IMPRINT",FACE,{"disambiguationData":[TD([[makeQuery(id+"F2.imprint","IMPRINT",EDGE,{"derivedFrom":sQuery(id+"F2.wireOp",EDGE,"E14.3.1")}),1.0]])]});
            var Q5;
            Q5=makeQuery(id+"F2.imprint","IMPRINT",FACE,{"disambiguationData":[TD([[makeQuery(id+"F2.imprint","IMPRINT",EDGE,{"derivedFrom":sQuery(id+"F2.wireOp",EDGE,"E14.2.1")}),1.0]])]});
            extrude(context, id + "F3", {"entities" : qUnion([Q0, Q1, Q2, Q3, Q4, Q5]), "operationType" : NewBodyOperationType.REMOVE, "endBound" : BoundingType.THROUGH_ALL, "oppositeDirection" : true, "depth" : 25.4 * mm});
        }
        {
            var Q0;
            Q0=makeQuery(id+"F2.imprint","IMPRINT",FACE,{"disambiguationData":[TD([[makeQuery(id+"F2.imprint","IMPRINT",EDGE,{"derivedFrom":sQuery(id+"F2.wireOp",EDGE,"E8")}),-1.0]])]});
            var Q1;
            Q1=makeQuery(id+"F2.imprint","IMPRINT",FACE,{"disambiguationData":[TD([[makeQuery(id+"F2.imprint","IMPRINT",EDGE,{"derivedFrom":sQuery(id+"F2.wireOp",EDGE,"E14.4.0")}),1.0]])]});
            var Q2;
            Q2=makeQuery(id+"F2.imprint","IMPRINT",FACE,{"disambiguationData":[TD([[makeQuery(id+"F2.imprint","IMPRINT",EDGE,{"derivedFrom":sQuery(id+"F2.wireOp",EDGE,"E14.3.0")}),1.0]])]});
            var Q3;
            Q3=makeQuery(id+"F2.imprint","IMPRINT",FACE,{"disambiguationData":[TD([[makeQuery(id+"F2.imprint","IMPRINT",EDGE,{"derivedFrom":sQuery(id+"F2.wireOp",EDGE,"E14.2.0")}),1.0]])]});
            var Q4;
            Q4=makeQuery(id+"F2.imprint","IMPRINT",FACE,{"disambiguationData":[TD([[makeQuery(id+"F2.imprint","IMPRINT",EDGE,{"derivedFrom":sQuery(id+"F2.wireOp",EDGE,"E14.1.0")}),1.0]])]});
            extrude(context, id + "F4", {"entities" : qUnion([Q0, Q1, Q2, Q3, Q4]), "operationType" : NewBodyOperationType.REMOVE, "oppositeDirection" : true, "depth" : 1.8 * mm});
        }
        {
            var Q0;
            Q0=makeQuery(id+"F1.opExtrude","CAP_FACE",FACE,{"disambiguationData":[OSD([sQuery(id+"F0.wireOp",EDGE,"E0"),sQuery(id+"F0.wireOp",EDGE,"E1"),sQuery(id+"F0.wireOp",EDGE,"E2"),sQuery(id+"F0.wireOp",EDGE,"E3.trimOffspring"),sQuery(id+"F0.wireOp",EDGE,"E5"),sQuery(id+"F0.wireOp",EDGE,"E7.1.4"),sQuery(id+"F0.wireOp",EDGE,"E7.1.5"),sQuery(id+"F0.wireOp",EDGE,"E7.1.6"),sQuery(id+"F0.wireOp",EDGE,"E7.1.7"),sQuery(id+"F0.wireOp",EDGE,"E7.1.8"),sQuery(id+"F0.wireOp",EDGE,"E7.2.4"),sQuery(id+"F0.wireOp",EDGE,"E7.2.5"),sQuery(id+"F0.wireOp",EDGE,"E7.2.6"),sQuery(id+"F0.wireOp",EDGE,"E7.2.7"),sQuery(id+"F0.wireOp",EDGE,"E7.2.8"),sQuery(id+"F0.wireOp",EDGE,"E7.3.4"),sQuery(id+"F0.wireOp",EDGE,"E7.3.5"),sQuery(id+"F0.wireOp",EDGE,"E7.3.6"),sQuery(id+"F0.wireOp",EDGE,"E7.3.7"),sQuery(id+"F0.wireOp",EDGE,"E7.3.8"),sQuery(id+"F0.wireOp",EDGE,"E7.4.4"),sQuery(id+"F0.wireOp",EDGE,"E7.4.5"),sQuery(id+"F0.wireOp",EDGE,"E7.4.6"),sQuery(id+"F0.wireOp",EDGE,"E7.4.7"),sQuery(id+"F0.wireOp",EDGE,"E7.4.8"),sQuery(id+"F0.wireOp",EDGE,"E7.5.4"),sQuery(id+"F0.wireOp",EDGE,"E7.5.5"),sQuery(id+"F0.wireOp",EDGE,"E7.5.6"),sQuery(id+"F0.wireOp",EDGE,"E7.5.7"),sQuery(id+"F0.wireOp",EDGE,"E7.5.8"),sQuery(id+"F0.wireOp",EDGE,"E7.6.4"),sQuery(id+"F0.wireOp",EDGE,"E7.6.5"),sQuery(id+"F0.wireOp",EDGE,"E7.6.6"),sQuery(id+"F0.wireOp",EDGE,"E7.6.7"),sQuery(id+"F0.wireOp",EDGE,"E7.6.8"),sQuery(id+"F0.wireOp",EDGE,"E7.7.4"),sQuery(id+"F0.wireOp",EDGE,"E7.7.5"),sQuery(id+"F0.wireOp",EDGE,"E7.7.6"),sQuery(id+"F0.wireOp",EDGE,"E7.7.7"),sQuery(id+"F0.wireOp",EDGE,"E7.7.8"),sQuery(id+"F0.wireOp",EDGE,"E7.8.4"),sQuery(id+"F0.wireOp",EDGE,"E7.8.5"),sQuery(id+"F0.wireOp",EDGE,"E7.8.6"),sQuery(id+"F0.wireOp",EDGE,"E7.8.7"),sQuery(id+"F0.wireOp",EDGE,"E7.8.8"),sQuery(id+"F0.wireOp",EDGE,"E7.9.4"),sQuery(id+"F0.wireOp",EDGE,"E7.9.5"),sQuery(id+"F0.wireOp",EDGE,"E7.9.6"),sQuery(id+"F0.wireOp",EDGE,"E7.9.7"),sQuery(id+"F0.wireOp",EDGE,"E7.9.8"),sQuery(id+"F0.wireOp",EDGE,"E7.10.4"),sQuery(id+"F0.wireOp",EDGE,"E7.10.5"),sQuery(id+"F0.wireOp",EDGE,"E7.10.6"),sQuery(id+"F0.wireOp",EDGE,"E7.10.7"),sQuery(id+"F0.wireOp",EDGE,"E7.10.8"),sQuery(id+"F0.wireOp",EDGE,"E7.11.4"),sQuery(id+"F0.wireOp",EDGE,"E7.11.5"),sQuery(id+"F0.wireOp",EDGE,"E7.11.6"),sQuery(id+"F0.wireOp",EDGE,"E7.11.7"),sQuery(id+"F0.wireOp",EDGE,"E7.11.8"),sQuery(id+"F0.wireOp",EDGE,"E7.12.4"),sQuery(id+"F0.wireOp",EDGE,"E7.12.5"),sQuery(id+"F0.wireOp",EDGE,"E7.12.6"),sQuery(id+"F0.wireOp",EDGE,"E7.12.7"),sQuery(id+"F0.wireOp",EDGE,"E7.12.8"),sQuery(id+"F0.wireOp",EDGE,"E7.13.4"),sQuery(id+"F0.wireOp",EDGE,"E7.13.5"),sQuery(id+"F0.wireOp",EDGE,"E7.13.6"),sQuery(id+"F0.wireOp",EDGE,"E7.13.7"),sQuery(id+"F0.wireOp",EDGE,"E7.13.8"),sQuery(id+"F0.wireOp",EDGE,"E7.14.4"),sQuery(id+"F0.wireOp",EDGE,"E7.14.5"),sQuery(id+"F0.wireOp",EDGE,"E7.14.6"),sQuery(id+"F0.wireOp",EDGE,"E7.14.7"),sQuery(id+"F0.wireOp",EDGE,"E7.14.8"),sQuery(id+"F0.wireOp",EDGE,"E7.15.4"),sQuery(id+"F0.wireOp",EDGE,"E7.15.5"),sQuery(id+"F0.wireOp",EDGE,"E7.15.6"),sQuery(id+"F0.wireOp",EDGE,"E7.15.7"),sQuery(id+"F0.wireOp",EDGE,"E7.15.8"),sQuery(id+"F0.wireOp",EDGE,"E7.16.4"),sQuery(id+"F0.wireOp",EDGE,"E7.16.5"),sQuery(id+"F0.wireOp",EDGE,"E7.16.6"),sQuery(id+"F0.wireOp",EDGE,"E7.16.7"),sQuery(id+"F0.wireOp",EDGE,"E7.16.8"),sQuery(id+"F0.wireOp",EDGE,"E7.17.4"),sQuery(id+"F0.wireOp",EDGE,"E7.17.5"),sQuery(id+"F0.wireOp",EDGE,"E7.17.6"),sQuery(id+"F0.wireOp",EDGE,"E7.17.7"),sQuery(id+"F0.wireOp",EDGE,"E7.17.8"),sQuery(id+"F0.wireOp",EDGE,"E7.18.4"),sQuery(id+"F0.wireOp",EDGE,"E7.18.5"),sQuery(id+"F0.wireOp",EDGE,"E7.18.6"),sQuery(id+"F0.wireOp",EDGE,"E7.18.7"),sQuery(id+"F0.wireOp",EDGE,"E7.18.8"),sQuery(id+"F0.wireOp",EDGE,"E7.19.4"),sQuery(id+"F0.wireOp",EDGE,"E7.19.5"),sQuery(id+"F0.wireOp",EDGE,"E7.19.6"),sQuery(id+"F0.wireOp",EDGE,"E7.19.7"),sQuery(id+"F0.wireOp",EDGE,"E7.19.8"),sQuery(id+"F0.wireOp",EDGE,"E7.20.4"),sQuery(id+"F0.wireOp",EDGE,"E7.20.5"),sQuery(id+"F0.wireOp",EDGE,"E7.20.6"),sQuery(id+"F0.wireOp",EDGE,"E7.20.7"),sQuery(id+"F0.wireOp",EDGE,"E7.20.8"),sQuery(id+"F0.wireOp",EDGE,"E7.21.4"),sQuery(id+"F0.wireOp",EDGE,"E7.21.5"),sQuery(id+"F0.wireOp",EDGE,"E7.21.6"),sQuery(id+"F0.wireOp",EDGE,"E7.21.7"),sQuery(id+"F0.wireOp",EDGE,"E7.21.8"),sQuery(id+"F0.wireOp",EDGE,"E7.22.4"),sQuery(id+"F0.wireOp",EDGE,"E7.22.5"),sQuery(id+"F0.wireOp",EDGE,"E7.22.6"),sQuery(id+"F0.wireOp",EDGE,"E7.22.7"),sQuery(id+"F0.wireOp",EDGE,"E7.22.8"),sQuery(id+"F0.wireOp",EDGE,"E7.23.4"),sQuery(id+"F0.wireOp",EDGE,"E7.23.5"),sQuery(id+"F0.wireOp",EDGE,"E7.23.6"),sQuery(id+"F0.wireOp",EDGE,"E7.23.7"),sQuery(id+"F0.wireOp",EDGE,"E7.23.8"),sQuery(id+"F0.wireOp",EDGE,"E7.24.4"),sQuery(id+"F0.wireOp",EDGE,"E7.24.5"),sQuery(id+"F0.wireOp",EDGE,"E7.24.6"),sQuery(id+"F0.wireOp",EDGE,"E7.24.7"),sQuery(id+"F0.wireOp",EDGE,"E7.24.8"),sQuery(id+"F0.wireOp",EDGE,"E7.25.4"),sQuery(id+"F0.wireOp",EDGE,"E7.25.5"),sQuery(id+"F0.wireOp",EDGE,"E7.25.6"),sQuery(id+"F0.wireOp",EDGE,"E7.25.7"),sQuery(id+"F0.wireOp",EDGE,"E7.25.8"),sQuery(id+"F0.wireOp",EDGE,"E7.26.4"),sQuery(id+"F0.wireOp",EDGE,"E7.26.5"),sQuery(id+"F0.wireOp",EDGE,"E7.26.6"),sQuery(id+"F0.wireOp",EDGE,"E7.26.7"),sQuery(id+"F0.wireOp",EDGE,"E7.26.8"),sQuery(id+"F0.wireOp",EDGE,"E7.27.4"),sQuery(id+"F0.wireOp",EDGE,"E7.27.5"),sQuery(id+"F0.wireOp",EDGE,"E7.27.6"),sQuery(id+"F0.wireOp",EDGE,"E7.27.7"),sQuery(id+"F0.wireOp",EDGE,"E7.27.8"),sQuery(id+"F0.wireOp",EDGE,"E7.28.4"),sQuery(id+"F0.wireOp",EDGE,"E7.28.5"),sQuery(id+"F0.wireOp",EDGE,"E7.28.6"),sQuery(id+"F0.wireOp",EDGE,"E7.28.7"),sQuery(id+"F0.wireOp",EDGE,"E7.28.8"),sQuery(id+"F0.wireOp",EDGE,"E7.29.4"),sQuery(id+"F0.wireOp",EDGE,"E7.29.5"),sQuery(id+"F0.wireOp",EDGE,"E7.29.6"),sQuery(id+"F0.wireOp",EDGE,"E7.29.7"),sQuery(id+"F0.wireOp",EDGE,"E7.29.8"),sQuery(id+"F0.wireOp",EDGE,"E7.30.4"),sQuery(id+"F0.wireOp",EDGE,"E7.30.5"),sQuery(id+"F0.wireOp",EDGE,"E7.30.6"),sQuery(id+"F0.wireOp",EDGE,"E7.30.7"),sQuery(id+"F0.wireOp",EDGE,"E7.30.8"),sQuery(id+"F0.wireOp",EDGE,"E7.31.4"),sQuery(id+"F0.wireOp",EDGE,"E7.31.5"),sQuery(id+"F0.wireOp",EDGE,"E7.31.6"),sQuery(id+"F0.wireOp",EDGE,"E7.31.7"),sQuery(id+"F0.wireOp",EDGE,"E7.31.8"),sQuery(id+"F0.wireOp",EDGE,"E7.32.4"),sQuery(id+"F0.wireOp",EDGE,"E7.32.5"),sQuery(id+"F0.wireOp",EDGE,"E7.32.6"),sQuery(id+"F0.wireOp",EDGE,"E7.32.7"),sQuery(id+"F0.wireOp",EDGE,"E7.32.8"),sQuery(id+"F0.wireOp",EDGE,"E7.33.4"),sQuery(id+"F0.wireOp",EDGE,"E7.33.5"),sQuery(id+"F0.wireOp",EDGE,"E7.33.6"),sQuery(id+"F0.wireOp",EDGE,"E7.33.7"),sQuery(id+"F0.wireOp",EDGE,"E7.33.8"),sQuery(id+"F0.wireOp",EDGE,"E7.34.4"),sQuery(id+"F0.wireOp",EDGE,"E7.34.5"),sQuery(id+"F0.wireOp",EDGE,"E7.34.6"),sQuery(id+"F0.wireOp",EDGE,"E7.34.7"),sQuery(id+"F0.wireOp",EDGE,"E7.34.8"),sQuery(id+"F0.wireOp",EDGE,"E7.35.4"),sQuery(id+"F0.wireOp",EDGE,"E7.35.5"),sQuery(id+"F0.wireOp",EDGE,"E7.35.6"),sQuery(id+"F0.wireOp",EDGE,"E7.35.7"),sQuery(id+"F0.wireOp",EDGE,"E7.35.8"),sQuery(id+"F0.wireOp",EDGE,"E7.36.4"),sQuery(id+"F0.wireOp",EDGE,"E7.36.5"),sQuery(id+"F0.wireOp",EDGE,"E7.36.6"),sQuery(id+"F0.wireOp",EDGE,"E7.36.7"),sQuery(id+"F0.wireOp",EDGE,"E7.36.8"),sQuery(id+"F0.wireOp",EDGE,"E7.37.4"),sQuery(id+"F0.wireOp",EDGE,"E7.37.5"),sQuery(id+"F0.wireOp",EDGE,"E7.37.6"),sQuery(id+"F0.wireOp",EDGE,"E7.37.7"),sQuery(id+"F0.wireOp",EDGE,"E7.37.8"),sQuery(id+"F0.wireOp",EDGE,"E7.38.4"),sQuery(id+"F0.wireOp",EDGE,"E7.38.5"),sQuery(id+"F0.wireOp",EDGE,"E7.38.6"),sQuery(id+"F0.wireOp",EDGE,"E7.38.7"),sQuery(id+"F0.wireOp",EDGE,"E7.38.8"),sQuery(id+"F0.wireOp",EDGE,"E7.39.4"),sQuery(id+"F0.wireOp",EDGE,"E7.39.5"),sQuery(id+"F0.wireOp",EDGE,"E7.39.6"),sQuery(id+"F0.wireOp",EDGE,"E7.39.7"),sQuery(id+"F0.wireOp",EDGE,"E7.39.8"),sQuery(id+"F0.wireOp",EDGE,"E7.40.4"),sQuery(id+"F0.wireOp",EDGE,"E7.40.5"),sQuery(id+"F0.wireOp",EDGE,"E7.40.6"),sQuery(id+"F0.wireOp",EDGE,"E7.40.7"),sQuery(id+"F0.wireOp",EDGE,"E7.40.8"),sQuery(id+"F0.wireOp",EDGE,"E7.41.4"),sQuery(id+"F0.wireOp",EDGE,"E7.41.5"),sQuery(id+"F0.wireOp",EDGE,"E7.41.6"),sQuery(id+"F0.wireOp",EDGE,"E7.41.7"),sQuery(id+"F0.wireOp",EDGE,"E7.41.8"),sQuery(id+"F0.wireOp",EDGE,"E7.42.4"),sQuery(id+"F0.wireOp",EDGE,"E7.42.5"),sQuery(id+"F0.wireOp",EDGE,"E7.42.6"),sQuery(id+"F0.wireOp",EDGE,"E7.42.7"),sQuery(id+"F0.wireOp",EDGE,"E7.42.8"),sQuery(id+"F0.wireOp",EDGE,"E7.43.4"),sQuery(id+"F0.wireOp",EDGE,"E7.43.5"),sQuery(id+"F0.wireOp",EDGE,"E7.43.6"),sQuery(id+"F0.wireOp",EDGE,"E7.43.7"),sQuery(id+"F0.wireOp",EDGE,"E7.43.8"),sQuery(id+"F0.wireOp",EDGE,"E7.44.4"),sQuery(id+"F0.wireOp",EDGE,"E7.44.5"),sQuery(id+"F0.wireOp",EDGE,"E7.44.6"),sQuery(id+"F0.wireOp",EDGE,"E7.44.7"),sQuery(id+"F0.wireOp",EDGE,"E7.44.8"),sQuery(id+"F0.wireOp",EDGE,"E7.45.4"),sQuery(id+"F0.wireOp",EDGE,"E7.45.5"),sQuery(id+"F0.wireOp",EDGE,"E7.45.6"),sQuery(id+"F0.wireOp",EDGE,"E7.45.7"),sQuery(id+"F0.wireOp",EDGE,"E7.45.8"),sQuery(id+"F0.wireOp",EDGE,"E7.46.4"),sQuery(id+"F0.wireOp",EDGE,"E7.46.5"),sQuery(id+"F0.wireOp",EDGE,"E7.46.6"),sQuery(id+"F0.wireOp",EDGE,"E7.46.7"),sQuery(id+"F0.wireOp",EDGE,"E7.46.8"),sQuery(id+"F0.wireOp",EDGE,"E7.47.4"),sQuery(id+"F0.wireOp",EDGE,"E7.47.5"),sQuery(id+"F0.wireOp",EDGE,"E7.47.6"),sQuery(id+"F0.wireOp",EDGE,"E7.47.7"),sQuery(id+"F0.wireOp",EDGE,"E7.47.8"),sQuery(id+"F0.wireOp",EDGE,"E7.48.4"),sQuery(id+"F0.wireOp",EDGE,"E7.48.5"),sQuery(id+"F0.wireOp",EDGE,"E7.48.6"),sQuery(id+"F0.wireOp",EDGE,"E7.48.7"),sQuery(id+"F0.wireOp",EDGE,"E7.48.8")])],"isStart":false});
            var sketch = newSketch(context, id + "F5", { "sketchPlane" : qUnion([Q0])});
            skCircle(sketch, "E15", {"center": v(0, 0) * mm, "radius": 92.14 * mm});
            skCircle(sketch, "E16", {"center": v(0, 0) * mm, "radius": 150 * mm});
            skSolve(sketch);
        }
        {
            var Q0;
            Q0 = qSketchRegion(id + "F5", true);
            extrude(context, id + "F6", {"entities" : qUnion([Q0]), "operationType" : NewBodyOperationType.REMOVE, "oppositeDirection" : true, "depth" : 0.35 * mm});
        }
        {
            var Q0;
            Q0=makeQuery(id+"F1.opExtrude","CAP_FACE",FACE,{"disambiguationData":[OSD([sQuery(id+"F0.wireOp",EDGE,"E0"),sQuery(id+"F0.wireOp",EDGE,"E1"),sQuery(id+"F0.wireOp",EDGE,"E2"),sQuery(id+"F0.wireOp",EDGE,"E3.trimOffspring"),sQuery(id+"F0.wireOp",EDGE,"E5"),sQuery(id+"F0.wireOp",EDGE,"E7.1.4"),sQuery(id+"F0.wireOp",EDGE,"E7.1.5"),sQuery(id+"F0.wireOp",EDGE,"E7.1.6"),sQuery(id+"F0.wireOp",EDGE,"E7.1.7"),sQuery(id+"F0.wireOp",EDGE,"E7.1.8"),sQuery(id+"F0.wireOp",EDGE,"E7.2.4"),sQuery(id+"F0.wireOp",EDGE,"E7.2.5"),sQuery(id+"F0.wireOp",EDGE,"E7.2.6"),sQuery(id+"F0.wireOp",EDGE,"E7.2.7"),sQuery(id+"F0.wireOp",EDGE,"E7.2.8"),sQuery(id+"F0.wireOp",EDGE,"E7.3.4"),sQuery(id+"F0.wireOp",EDGE,"E7.3.5"),sQuery(id+"F0.wireOp",EDGE,"E7.3.6"),sQuery(id+"F0.wireOp",EDGE,"E7.3.7"),sQuery(id+"F0.wireOp",EDGE,"E7.3.8"),sQuery(id+"F0.wireOp",EDGE,"E7.4.4"),sQuery(id+"F0.wireOp",EDGE,"E7.4.5"),sQuery(id+"F0.wireOp",EDGE,"E7.4.6"),sQuery(id+"F0.wireOp",EDGE,"E7.4.7"),sQuery(id+"F0.wireOp",EDGE,"E7.4.8"),sQuery(id+"F0.wireOp",EDGE,"E7.5.4"),sQuery(id+"F0.wireOp",EDGE,"E7.5.5"),sQuery(id+"F0.wireOp",EDGE,"E7.5.6"),sQuery(id+"F0.wireOp",EDGE,"E7.5.7"),sQuery(id+"F0.wireOp",EDGE,"E7.5.8"),sQuery(id+"F0.wireOp",EDGE,"E7.6.4"),sQuery(id+"F0.wireOp",EDGE,"E7.6.5"),sQuery(id+"F0.wireOp",EDGE,"E7.6.6"),sQuery(id+"F0.wireOp",EDGE,"E7.6.7"),sQuery(id+"F0.wireOp",EDGE,"E7.6.8"),sQuery(id+"F0.wireOp",EDGE,"E7.7.4"),sQuery(id+"F0.wireOp",EDGE,"E7.7.5"),sQuery(id+"F0.wireOp",EDGE,"E7.7.6"),sQuery(id+"F0.wireOp",EDGE,"E7.7.7"),sQuery(id+"F0.wireOp",EDGE,"E7.7.8"),sQuery(id+"F0.wireOp",EDGE,"E7.8.4"),sQuery(id+"F0.wireOp",EDGE,"E7.8.5"),sQuery(id+"F0.wireOp",EDGE,"E7.8.6"),sQuery(id+"F0.wireOp",EDGE,"E7.8.7"),sQuery(id+"F0.wireOp",EDGE,"E7.8.8"),sQuery(id+"F0.wireOp",EDGE,"E7.9.4"),sQuery(id+"F0.wireOp",EDGE,"E7.9.5"),sQuery(id+"F0.wireOp",EDGE,"E7.9.6"),sQuery(id+"F0.wireOp",EDGE,"E7.9.7"),sQuery(id+"F0.wireOp",EDGE,"E7.9.8"),sQuery(id+"F0.wireOp",EDGE,"E7.10.4"),sQuery(id+"F0.wireOp",EDGE,"E7.10.5"),sQuery(id+"F0.wireOp",EDGE,"E7.10.6"),sQuery(id+"F0.wireOp",EDGE,"E7.10.7"),sQuery(id+"F0.wireOp",EDGE,"E7.10.8"),sQuery(id+"F0.wireOp",EDGE,"E7.11.4"),sQuery(id+"F0.wireOp",EDGE,"E7.11.5"),sQuery(id+"F0.wireOp",EDGE,"E7.11.6"),sQuery(id+"F0.wireOp",EDGE,"E7.11.7"),sQuery(id+"F0.wireOp",EDGE,"E7.11.8"),sQuery(id+"F0.wireOp",EDGE,"E7.12.4"),sQuery(id+"F0.wireOp",EDGE,"E7.12.5"),sQuery(id+"F0.wireOp",EDGE,"E7.12.6"),sQuery(id+"F0.wireOp",EDGE,"E7.12.7"),sQuery(id+"F0.wireOp",EDGE,"E7.12.8"),sQuery(id+"F0.wireOp",EDGE,"E7.13.4"),sQuery(id+"F0.wireOp",EDGE,"E7.13.5"),sQuery(id+"F0.wireOp",EDGE,"E7.13.6"),sQuery(id+"F0.wireOp",EDGE,"E7.13.7"),sQuery(id+"F0.wireOp",EDGE,"E7.13.8"),sQuery(id+"F0.wireOp",EDGE,"E7.14.4"),sQuery(id+"F0.wireOp",EDGE,"E7.14.5"),sQuery(id+"F0.wireOp",EDGE,"E7.14.6"),sQuery(id+"F0.wireOp",EDGE,"E7.14.7"),sQuery(id+"F0.wireOp",EDGE,"E7.14.8"),sQuery(id+"F0.wireOp",EDGE,"E7.15.4"),sQuery(id+"F0.wireOp",EDGE,"E7.15.5"),sQuery(id+"F0.wireOp",EDGE,"E7.15.6"),sQuery(id+"F0.wireOp",EDGE,"E7.15.7"),sQuery(id+"F0.wireOp",EDGE,"E7.15.8"),sQuery(id+"F0.wireOp",EDGE,"E7.16.4"),sQuery(id+"F0.wireOp",EDGE,"E7.16.5"),sQuery(id+"F0.wireOp",EDGE,"E7.16.6"),sQuery(id+"F0.wireOp",EDGE,"E7.16.7"),sQuery(id+"F0.wireOp",EDGE,"E7.16.8"),sQuery(id+"F0.wireOp",EDGE,"E7.17.4"),sQuery(id+"F0.wireOp",EDGE,"E7.17.5"),sQuery(id+"F0.wireOp",EDGE,"E7.17.6"),sQuery(id+"F0.wireOp",EDGE,"E7.17.7"),sQuery(id+"F0.wireOp",EDGE,"E7.17.8"),sQuery(id+"F0.wireOp",EDGE,"E7.18.4"),sQuery(id+"F0.wireOp",EDGE,"E7.18.5"),sQuery(id+"F0.wireOp",EDGE,"E7.18.6"),sQuery(id+"F0.wireOp",EDGE,"E7.18.7"),sQuery(id+"F0.wireOp",EDGE,"E7.18.8"),sQuery(id+"F0.wireOp",EDGE,"E7.19.4"),sQuery(id+"F0.wireOp",EDGE,"E7.19.5"),sQuery(id+"F0.wireOp",EDGE,"E7.19.6"),sQuery(id+"F0.wireOp",EDGE,"E7.19.7"),sQuery(id+"F0.wireOp",EDGE,"E7.19.8"),sQuery(id+"F0.wireOp",EDGE,"E7.20.4"),sQuery(id+"F0.wireOp",EDGE,"E7.20.5"),sQuery(id+"F0.wireOp",EDGE,"E7.20.6"),sQuery(id+"F0.wireOp",EDGE,"E7.20.7"),sQuery(id+"F0.wireOp",EDGE,"E7.20.8"),sQuery(id+"F0.wireOp",EDGE,"E7.21.4"),sQuery(id+"F0.wireOp",EDGE,"E7.21.5"),sQuery(id+"F0.wireOp",EDGE,"E7.21.6"),sQuery(id+"F0.wireOp",EDGE,"E7.21.7"),sQuery(id+"F0.wireOp",EDGE,"E7.21.8"),sQuery(id+"F0.wireOp",EDGE,"E7.22.4"),sQuery(id+"F0.wireOp",EDGE,"E7.22.5"),sQuery(id+"F0.wireOp",EDGE,"E7.22.6"),sQuery(id+"F0.wireOp",EDGE,"E7.22.7"),sQuery(id+"F0.wireOp",EDGE,"E7.22.8"),sQuery(id+"F0.wireOp",EDGE,"E7.23.4"),sQuery(id+"F0.wireOp",EDGE,"E7.23.5"),sQuery(id+"F0.wireOp",EDGE,"E7.23.6"),sQuery(id+"F0.wireOp",EDGE,"E7.23.7"),sQuery(id+"F0.wireOp",EDGE,"E7.23.8"),sQuery(id+"F0.wireOp",EDGE,"E7.24.4"),sQuery(id+"F0.wireOp",EDGE,"E7.24.5"),sQuery(id+"F0.wireOp",EDGE,"E7.24.6"),sQuery(id+"F0.wireOp",EDGE,"E7.24.7"),sQuery(id+"F0.wireOp",EDGE,"E7.24.8"),sQuery(id+"F0.wireOp",EDGE,"E7.25.4"),sQuery(id+"F0.wireOp",EDGE,"E7.25.5"),sQuery(id+"F0.wireOp",EDGE,"E7.25.6"),sQuery(id+"F0.wireOp",EDGE,"E7.25.7"),sQuery(id+"F0.wireOp",EDGE,"E7.25.8"),sQuery(id+"F0.wireOp",EDGE,"E7.26.4"),sQuery(id+"F0.wireOp",EDGE,"E7.26.5"),sQuery(id+"F0.wireOp",EDGE,"E7.26.6"),sQuery(id+"F0.wireOp",EDGE,"E7.26.7"),sQuery(id+"F0.wireOp",EDGE,"E7.26.8"),sQuery(id+"F0.wireOp",EDGE,"E7.27.4"),sQuery(id+"F0.wireOp",EDGE,"E7.27.5"),sQuery(id+"F0.wireOp",EDGE,"E7.27.6"),sQuery(id+"F0.wireOp",EDGE,"E7.27.7"),sQuery(id+"F0.wireOp",EDGE,"E7.27.8"),sQuery(id+"F0.wireOp",EDGE,"E7.28.4"),sQuery(id+"F0.wireOp",EDGE,"E7.28.5"),sQuery(id+"F0.wireOp",EDGE,"E7.28.6"),sQuery(id+"F0.wireOp",EDGE,"E7.28.7"),sQuery(id+"F0.wireOp",EDGE,"E7.28.8"),sQuery(id+"F0.wireOp",EDGE,"E7.29.4"),sQuery(id+"F0.wireOp",EDGE,"E7.29.5"),sQuery(id+"F0.wireOp",EDGE,"E7.29.6"),sQuery(id+"F0.wireOp",EDGE,"E7.29.7"),sQuery(id+"F0.wireOp",EDGE,"E7.29.8"),sQuery(id+"F0.wireOp",EDGE,"E7.30.4"),sQuery(id+"F0.wireOp",EDGE,"E7.30.5"),sQuery(id+"F0.wireOp",EDGE,"E7.30.6"),sQuery(id+"F0.wireOp",EDGE,"E7.30.7"),sQuery(id+"F0.wireOp",EDGE,"E7.30.8"),sQuery(id+"F0.wireOp",EDGE,"E7.31.4"),sQuery(id+"F0.wireOp",EDGE,"E7.31.5"),sQuery(id+"F0.wireOp",EDGE,"E7.31.6"),sQuery(id+"F0.wireOp",EDGE,"E7.31.7"),sQuery(id+"F0.wireOp",EDGE,"E7.31.8"),sQuery(id+"F0.wireOp",EDGE,"E7.32.4"),sQuery(id+"F0.wireOp",EDGE,"E7.32.5"),sQuery(id+"F0.wireOp",EDGE,"E7.32.6"),sQuery(id+"F0.wireOp",EDGE,"E7.32.7"),sQuery(id+"F0.wireOp",EDGE,"E7.32.8"),sQuery(id+"F0.wireOp",EDGE,"E7.33.4"),sQuery(id+"F0.wireOp",EDGE,"E7.33.5"),sQuery(id+"F0.wireOp",EDGE,"E7.33.6"),sQuery(id+"F0.wireOp",EDGE,"E7.33.7"),sQuery(id+"F0.wireOp",EDGE,"E7.33.8"),sQuery(id+"F0.wireOp",EDGE,"E7.34.4"),sQuery(id+"F0.wireOp",EDGE,"E7.34.5"),sQuery(id+"F0.wireOp",EDGE,"E7.34.6"),sQuery(id+"F0.wireOp",EDGE,"E7.34.7"),sQuery(id+"F0.wireOp",EDGE,"E7.34.8"),sQuery(id+"F0.wireOp",EDGE,"E7.35.4"),sQuery(id+"F0.wireOp",EDGE,"E7.35.5"),sQuery(id+"F0.wireOp",EDGE,"E7.35.6"),sQuery(id+"F0.wireOp",EDGE,"E7.35.7"),sQuery(id+"F0.wireOp",EDGE,"E7.35.8"),sQuery(id+"F0.wireOp",EDGE,"E7.36.4"),sQuery(id+"F0.wireOp",EDGE,"E7.36.5"),sQuery(id+"F0.wireOp",EDGE,"E7.36.6"),sQuery(id+"F0.wireOp",EDGE,"E7.36.7"),sQuery(id+"F0.wireOp",EDGE,"E7.36.8"),sQuery(id+"F0.wireOp",EDGE,"E7.37.4"),sQuery(id+"F0.wireOp",EDGE,"E7.37.5"),sQuery(id+"F0.wireOp",EDGE,"E7.37.6"),sQuery(id+"F0.wireOp",EDGE,"E7.37.7"),sQuery(id+"F0.wireOp",EDGE,"E7.37.8"),sQuery(id+"F0.wireOp",EDGE,"E7.38.4"),sQuery(id+"F0.wireOp",EDGE,"E7.38.5"),sQuery(id+"F0.wireOp",EDGE,"E7.38.6"),sQuery(id+"F0.wireOp",EDGE,"E7.38.7"),sQuery(id+"F0.wireOp",EDGE,"E7.38.8"),sQuery(id+"F0.wireOp",EDGE,"E7.39.4"),sQuery(id+"F0.wireOp",EDGE,"E7.39.5"),sQuery(id+"F0.wireOp",EDGE,"E7.39.6"),sQuery(id+"F0.wireOp",EDGE,"E7.39.7"),sQuery(id+"F0.wireOp",EDGE,"E7.39.8"),sQuery(id+"F0.wireOp",EDGE,"E7.40.4"),sQuery(id+"F0.wireOp",EDGE,"E7.40.5"),sQuery(id+"F0.wireOp",EDGE,"E7.40.6"),sQuery(id+"F0.wireOp",EDGE,"E7.40.7"),sQuery(id+"F0.wireOp",EDGE,"E7.40.8"),sQuery(id+"F0.wireOp",EDGE,"E7.41.4"),sQuery(id+"F0.wireOp",EDGE,"E7.41.5"),sQuery(id+"F0.wireOp",EDGE,"E7.41.6"),sQuery(id+"F0.wireOp",EDGE,"E7.41.7"),sQuery(id+"F0.wireOp",EDGE,"E7.41.8"),sQuery(id+"F0.wireOp",EDGE,"E7.42.4"),sQuery(id+"F0.wireOp",EDGE,"E7.42.5"),sQuery(id+"F0.wireOp",EDGE,"E7.42.6"),sQuery(id+"F0.wireOp",EDGE,"E7.42.7"),sQuery(id+"F0.wireOp",EDGE,"E7.42.8"),sQuery(id+"F0.wireOp",EDGE,"E7.43.4"),sQuery(id+"F0.wireOp",EDGE,"E7.43.5"),sQuery(id+"F0.wireOp",EDGE,"E7.43.6"),sQuery(id+"F0.wireOp",EDGE,"E7.43.7"),sQuery(id+"F0.wireOp",EDGE,"E7.43.8"),sQuery(id+"F0.wireOp",EDGE,"E7.44.4"),sQuery(id+"F0.wireOp",EDGE,"E7.44.5"),sQuery(id+"F0.wireOp",EDGE,"E7.44.6"),sQuery(id+"F0.wireOp",EDGE,"E7.44.7"),sQuery(id+"F0.wireOp",EDGE,"E7.44.8"),sQuery(id+"F0.wireOp",EDGE,"E7.45.4"),sQuery(id+"F0.wireOp",EDGE,"E7.45.5"),sQuery(id+"F0.wireOp",EDGE,"E7.45.6"),sQuery(id+"F0.wireOp",EDGE,"E7.45.7"),sQuery(id+"F0.wireOp",EDGE,"E7.45.8"),sQuery(id+"F0.wireOp",EDGE,"E7.46.4"),sQuery(id+"F0.wireOp",EDGE,"E7.46.5"),sQuery(id+"F0.wireOp",EDGE,"E7.46.6"),sQuery(id+"F0.wireOp",EDGE,"E7.46.7"),sQuery(id+"F0.wireOp",EDGE,"E7.46.8"),sQuery(id+"F0.wireOp",EDGE,"E7.47.4"),sQuery(id+"F0.wireOp",EDGE,"E7.47.5"),sQuery(id+"F0.wireOp",EDGE,"E7.47.6"),sQuery(id+"F0.wireOp",EDGE,"E7.47.7"),sQuery(id+"F0.wireOp",EDGE,"E7.47.8"),sQuery(id+"F0.wireOp",EDGE,"E7.48.4"),sQuery(id+"F0.wireOp",EDGE,"E7.48.5"),sQuery(id+"F0.wireOp",EDGE,"E7.48.6"),sQuery(id+"F0.wireOp",EDGE,"E7.48.7"),sQuery(id+"F0.wireOp",EDGE,"E7.48.8")])],"isStart":true});
            var sketch = newSketch(context, id + "F7", { "sketchPlane" : qUnion([Q0])});
            skCircle(sketch, "E17", {"center": v(0, 0) * mm, "radius": 92.14 * mm});
            skCircle(sketch, "E18", {"center": v(0, 0) * mm, "radius": 150 * mm});
            skSolve(sketch);
        }
        {
            var Q0;
            Q0 = qSketchRegion(id + "F7", true);
            extrude(context, id + "F8", {"entities" : qUnion([Q0]), "operationType" : NewBodyOperationType.REMOVE, "oppositeDirection" : true, "depth" : 0.35 * mm});
        }
        {
            var Q0;
            Q0=qCreatedBy(makeId("Front.planeOp"),FACE);
            var sketch = newSketch(context, id + "F9", { "sketchPlane" : qUnion([Q0])});
            skLineSegment(sketch, "E19", {"start": v(105, 2.2) * mm, "end": v(98, 3.5) * mm});
            skLineSegment(sketch, "E20", {"start": v(98, 3.5) * mm, "end": v(105, 3.5) * mm});
            skLineSegment(sketch, "E21", {"start": v(105, 3.5) * mm, "end": v(105, 2.2) * mm});
            skLineSegment(sketch, "E22", {"start": v(105, 1.3) * mm, "end": v(105, 0) * mm});
            skLineSegment(sketch, "E23", {"start": v(105, 0) * mm, "end": v(98, 0) * mm});
            skLineSegment(sketch, "E24", {"start": v(98, 0) * mm, "end": v(105, 1.3) * mm});
            skLineSegment(sketch, "E25", {"start": v(0, 0) * mm, "end": v(0, 19.85) * mm, "construction": true});
            skSolve(sketch);
        }
        {
            var Q0;
            Q0 = qSketchRegion(id + "F9", true);
            var Q1;
            Q1=sQuery(id+"F9.wireOp",EDGE,"E25");
            revolve(context, id + "F10", {"operationType" : NewBodyOperationType.REMOVE, "entities" : qUnion([Q0]), "axis" : qUnion([Q1]), "revolveType" : RevolveType.FULL, "oppositeDirection" : true});
        }
    });
